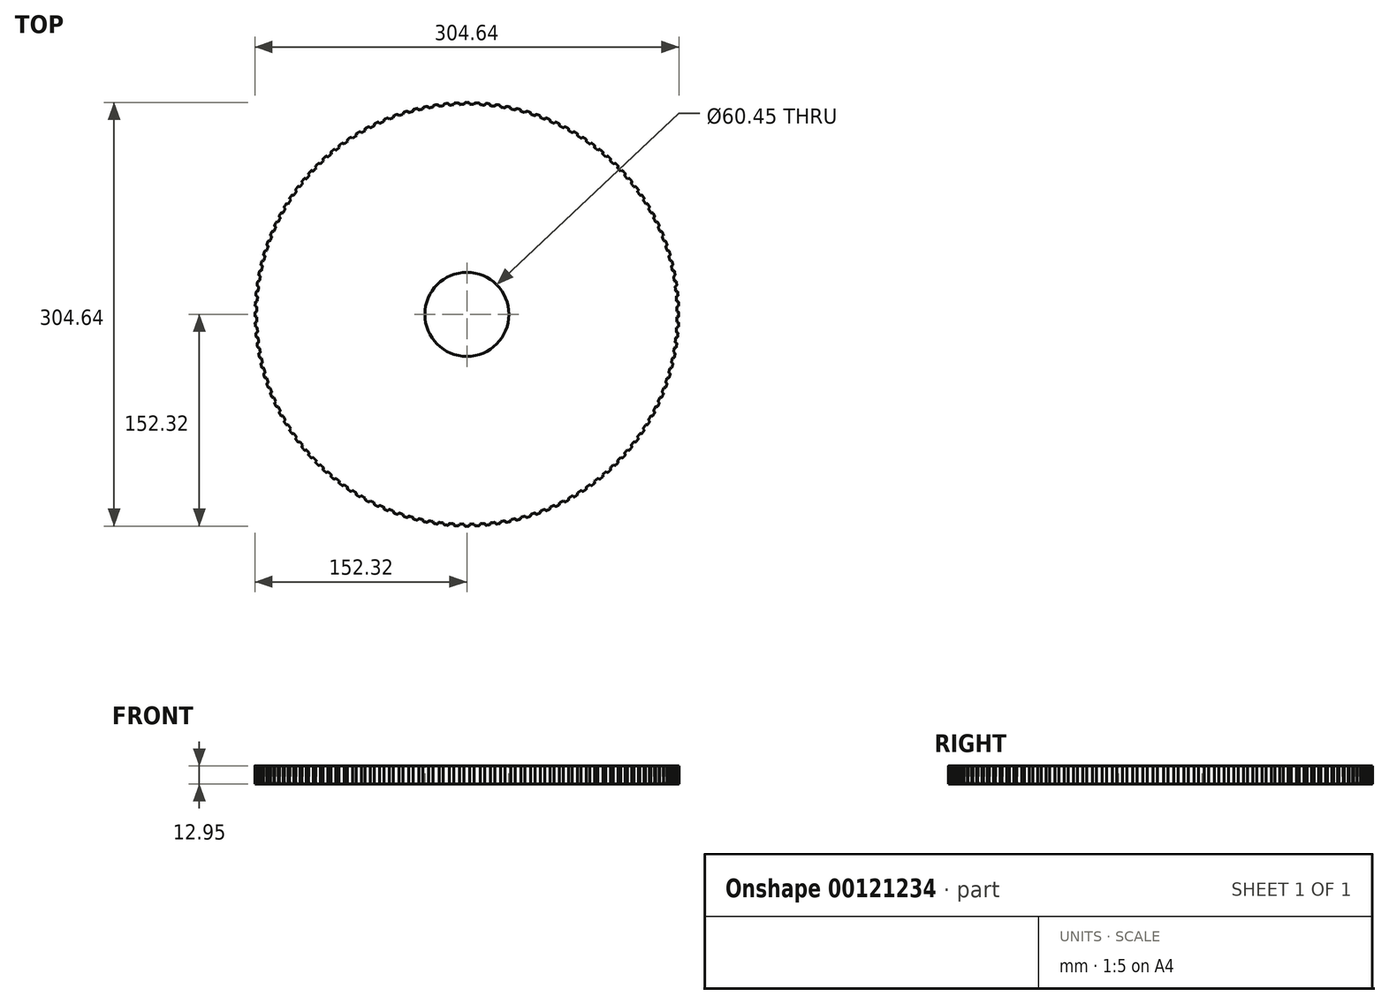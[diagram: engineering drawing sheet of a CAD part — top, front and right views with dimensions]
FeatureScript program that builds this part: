
annotation { "Feature Type Name" : "Feature", "Feature Type Description" : "" }
export const myFeature = defineFeature(function(context is Context, id is Id, definition is map)
    precondition{}
    {
        {
            var Q0;
            Q0=qCreatedBy(makeId("Top.planeOp"),FACE);
            var sketch = newSketch(context, id + "F0", { "sketchPlane" : qUnion([Q0])});
            skCircle(sketch, "E0", {"center": v(0, 0) * mm, "radius": 151 * mm});
            skSolve(sketch);
        }
        {
            var Q0;
            Q0 = qSketchRegion(id + "F0", true);
            extrude(context, id + "F1", {"entities" : qUnion([Q0]), "depth" : 12.95 * mm});
        }
        {
            var Q0;
            Q0=qCreatedBy(makeId("Top.planeOp"),FACE);
            var sketch = newSketch(context, id + "F2", { "sketchPlane" : qUnion([Q0])});
            skLineSegment(sketch, "E1", {"start": v(0, -0.08) * mm, "end": v(0, 183.08) * mm, "construction": true});
            skArc(sketch, "E2", {"start": v(1.26, 152.32) * mm, "mid": v(0, 152.32) * mm, "end": v(-1.26, 152.32) * mm});
            skLineSegment(sketch, "E3", {"start": v(-1.6, 152.1) * mm, "end": v(-2.1, 151.02) * mm});
            skLineSegment(sketch, "E4", {"start": v(1.6, 152.1) * mm, "end": v(2.1, 151.02) * mm});
            skPoint(sketch, "E5.visualSharp", {"position": v(-1.5, 152.32) * mm});
            skArc(sketch, "E5.filletArc", {"start": v(-1.26, 152.32) * mm, "mid": v(-1.46, 152.26) * mm, "end": v(-1.6, 152.1) * mm});
            skPoint(sketch, "E6.visualSharp", {"position": v(1.5, 152.32) * mm});
            skArc(sketch, "E6.filletArc", {"start": v(1.6, 152.1) * mm, "mid": v(1.46, 152.26) * mm, "end": v(1.26, 152.32) * mm});
            skArc(sketch, "E7", {"start": v(-2.27, 150.9) * mm, "mid": v(-2.17, 150.94) * mm, "end": v(-2.1, 151.02) * mm});
            skArc(sketch, "E8", {"start": v(2.1, 151.02) * mm, "mid": v(2.17, 150.94) * mm, "end": v(2.27, 150.9) * mm});
            skPoint(sketch, "E9.orphan", {"position": v(2.15, 150.91) * mm});
            skArc(sketch, "E10", {"start": v(-2.27, 150.9) * mm, "mid": v(0, 150.67) * mm, "end": v(2.27, 150.9) * mm});
            skSolve(sketch);
        }
        {
            var Q0;
            Q0=makeQuery(id+"F2.imprint","IMPRINT",FACE,{"disambiguationData":[TD([[makeQuery(id+"F2.imprint","IMPRINT",EDGE,{"derivedFrom":sQuery(id+"F2.wireOp",EDGE,"E2")}),1.0]])]});
            var Q1;
            Q1=makeQuery(id+"F2.imprint","IMPRINT",FACE,{"disambiguationData":[TD([[makeQuery(id+"F2.imprint","IMPRINT",EDGE,{"derivedFrom":sQuery(id+"F2.wireOp",EDGE,"bbfa1fc5-6552-4957-9194-8f10230bb92c.0")}),1.0]])]});
            var Q2;
            Q2=makeQuery(id+"F1.opExtrude","CAP_FACE",FACE,{"disambiguationData":[OSD([sQuery(id+"F0.wireOp",EDGE,"E0")])],"isStart":false});
            extrude(context, id + "F3", {"entities" : qUnion([Q0, Q1]), "endBound" : BoundingType.UP_TO_SURFACE, "endBoundEntityFace" : qUnion([Q2]), "depth" : 25.4 * mm});
        }
        {
            var Q0;
            Q0=qCreatedBy(makeId("Front.planeOp"),FACE);
            var sketch = newSketch(context, id + "F4", { "sketchPlane" : qUnion([Q0])});
            skLineSegment(sketch, "E11", {"start": v(0, 74.48) * mm, "end": v(0, -67.78) * mm, "construction": true});
            skSolve(sketch);
        }
        {
            var Q0;
            Q0=makeQuery(id+"F3.opExtrude","SWEPT_BODY",BODY,{"disambiguationData":[OSD([sQuery(id+"F2.wireOp",EDGE,"E2"),sQuery(id+"F2.wireOp",EDGE,"E3"),sQuery(id+"F2.wireOp",EDGE,"E4"),sQuery(id+"F2.wireOp",EDGE,"E5.filletArc"),sQuery(id+"F2.wireOp",EDGE,"E6.filletArc"),sQuery(id+"F2.wireOp",EDGE,"E7"),sQuery(id+"F2.wireOp",EDGE,"E8"),sQuery(id+"F2.wireOp",EDGE,"E10")])]});
            var Q1;
            Q1=sQuery(id+"F4.wireOp",EDGE,"E11");
            circularPattern(context, id + "F5", {"entities" : qUnion([Q0]), "axis" : qUnion([Q1]), "angle" : 360 * degree, "instanceCount" : 128, "equalSpace" : true});
        }
        {
            var Q0;
            Q0=makeQuery(id+"F1.opExtrude","SWEPT_BODY",BODY,{"disambiguationData":[OSD([sQuery(id+"F0.wireOp",EDGE,"E0")])]});
            var Q1;
            Q1=makeQuery(id+"F3.opExtrude","SWEPT_BODY",BODY,{"disambiguationData":[OSD([sQuery(id+"F2.wireOp",EDGE,"E2"),sQuery(id+"F2.wireOp",EDGE,"E3"),sQuery(id+"F2.wireOp",EDGE,"E4"),sQuery(id+"F2.wireOp",EDGE,"E5.filletArc"),sQuery(id+"F2.wireOp",EDGE,"E6.filletArc"),sQuery(id+"F2.wireOp",EDGE,"E7"),sQuery(id+"F2.wireOp",EDGE,"E8"),sQuery(id+"F2.wireOp",EDGE,"E10")])]});
            var Q2;
            Q2=makeQuery(id+"F5.opPattern","COPY",BODY,{"derivedFrom":makeQuery(id+"F3.opExtrude","SWEPT_BODY",BODY,{"disambiguationData":[OSD([sQuery(id+"F2.wireOp",EDGE,"E2"),sQuery(id+"F2.wireOp",EDGE,"E3"),sQuery(id+"F2.wireOp",EDGE,"E4"),sQuery(id+"F2.wireOp",EDGE,"E5.filletArc"),sQuery(id+"F2.wireOp",EDGE,"E6.filletArc"),sQuery(id+"F2.wireOp",EDGE,"E7"),sQuery(id+"F2.wireOp",EDGE,"E8"),sQuery(id+"F2.wireOp",EDGE,"E10")])]}),"instanceName":"1"});
            var Q3;
            Q3=makeQuery(id+"F5.opPattern","COPY",BODY,{"derivedFrom":makeQuery(id+"F3.opExtrude","SWEPT_BODY",BODY,{"disambiguationData":[OSD([sQuery(id+"F2.wireOp",EDGE,"E2"),sQuery(id+"F2.wireOp",EDGE,"E3"),sQuery(id+"F2.wireOp",EDGE,"E4"),sQuery(id+"F2.wireOp",EDGE,"E5.filletArc"),sQuery(id+"F2.wireOp",EDGE,"E6.filletArc"),sQuery(id+"F2.wireOp",EDGE,"E7"),sQuery(id+"F2.wireOp",EDGE,"E8"),sQuery(id+"F2.wireOp",EDGE,"E10")])]}),"instanceName":"2"});
            var Q4;
            Q4=makeQuery(id+"F5.opPattern","COPY",BODY,{"derivedFrom":makeQuery(id+"F3.opExtrude","SWEPT_BODY",BODY,{"disambiguationData":[OSD([sQuery(id+"F2.wireOp",EDGE,"E2"),sQuery(id+"F2.wireOp",EDGE,"E3"),sQuery(id+"F2.wireOp",EDGE,"E4"),sQuery(id+"F2.wireOp",EDGE,"E5.filletArc"),sQuery(id+"F2.wireOp",EDGE,"E6.filletArc"),sQuery(id+"F2.wireOp",EDGE,"E7"),sQuery(id+"F2.wireOp",EDGE,"E8"),sQuery(id+"F2.wireOp",EDGE,"E10")])]}),"instanceName":"3"});
            var Q5;
            Q5=makeQuery(id+"F5.opPattern","COPY",BODY,{"derivedFrom":makeQuery(id+"F3.opExtrude","SWEPT_BODY",BODY,{"disambiguationData":[OSD([sQuery(id+"F2.wireOp",EDGE,"E2"),sQuery(id+"F2.wireOp",EDGE,"E3"),sQuery(id+"F2.wireOp",EDGE,"E4"),sQuery(id+"F2.wireOp",EDGE,"E5.filletArc"),sQuery(id+"F2.wireOp",EDGE,"E6.filletArc"),sQuery(id+"F2.wireOp",EDGE,"E7"),sQuery(id+"F2.wireOp",EDGE,"E8"),sQuery(id+"F2.wireOp",EDGE,"E10")])]}),"instanceName":"4"});
            var Q6;
            Q6=makeQuery(id+"F5.opPattern","COPY",BODY,{"derivedFrom":makeQuery(id+"F3.opExtrude","SWEPT_BODY",BODY,{"disambiguationData":[OSD([sQuery(id+"F2.wireOp",EDGE,"E2"),sQuery(id+"F2.wireOp",EDGE,"E3"),sQuery(id+"F2.wireOp",EDGE,"E4"),sQuery(id+"F2.wireOp",EDGE,"E5.filletArc"),sQuery(id+"F2.wireOp",EDGE,"E6.filletArc"),sQuery(id+"F2.wireOp",EDGE,"E7"),sQuery(id+"F2.wireOp",EDGE,"E8"),sQuery(id+"F2.wireOp",EDGE,"E10")])]}),"instanceName":"5"});
            var Q7;
            Q7=makeQuery(id+"F5.opPattern","COPY",BODY,{"derivedFrom":makeQuery(id+"F3.opExtrude","SWEPT_BODY",BODY,{"disambiguationData":[OSD([sQuery(id+"F2.wireOp",EDGE,"E2"),sQuery(id+"F2.wireOp",EDGE,"E3"),sQuery(id+"F2.wireOp",EDGE,"E4"),sQuery(id+"F2.wireOp",EDGE,"E5.filletArc"),sQuery(id+"F2.wireOp",EDGE,"E6.filletArc"),sQuery(id+"F2.wireOp",EDGE,"E7"),sQuery(id+"F2.wireOp",EDGE,"E8"),sQuery(id+"F2.wireOp",EDGE,"E10")])]}),"instanceName":"6"});
            var Q8;
            Q8=makeQuery(id+"F5.opPattern","COPY",BODY,{"derivedFrom":makeQuery(id+"F3.opExtrude","SWEPT_BODY",BODY,{"disambiguationData":[OSD([sQuery(id+"F2.wireOp",EDGE,"E2"),sQuery(id+"F2.wireOp",EDGE,"E3"),sQuery(id+"F2.wireOp",EDGE,"E4"),sQuery(id+"F2.wireOp",EDGE,"E5.filletArc"),sQuery(id+"F2.wireOp",EDGE,"E6.filletArc"),sQuery(id+"F2.wireOp",EDGE,"E7"),sQuery(id+"F2.wireOp",EDGE,"E8"),sQuery(id+"F2.wireOp",EDGE,"E10")])]}),"instanceName":"7"});
            var Q9;
            Q9=makeQuery(id+"F5.opPattern","COPY",BODY,{"derivedFrom":makeQuery(id+"F3.opExtrude","SWEPT_BODY",BODY,{"disambiguationData":[OSD([sQuery(id+"F2.wireOp",EDGE,"E2"),sQuery(id+"F2.wireOp",EDGE,"E3"),sQuery(id+"F2.wireOp",EDGE,"E4"),sQuery(id+"F2.wireOp",EDGE,"E5.filletArc"),sQuery(id+"F2.wireOp",EDGE,"E6.filletArc"),sQuery(id+"F2.wireOp",EDGE,"E7"),sQuery(id+"F2.wireOp",EDGE,"E8"),sQuery(id+"F2.wireOp",EDGE,"E10")])]}),"instanceName":"8"});
            var Q10;
            Q10=makeQuery(id+"F5.opPattern","COPY",BODY,{"derivedFrom":makeQuery(id+"F3.opExtrude","SWEPT_BODY",BODY,{"disambiguationData":[OSD([sQuery(id+"F2.wireOp",EDGE,"E2"),sQuery(id+"F2.wireOp",EDGE,"E3"),sQuery(id+"F2.wireOp",EDGE,"E4"),sQuery(id+"F2.wireOp",EDGE,"E5.filletArc"),sQuery(id+"F2.wireOp",EDGE,"E6.filletArc"),sQuery(id+"F2.wireOp",EDGE,"E7"),sQuery(id+"F2.wireOp",EDGE,"E8"),sQuery(id+"F2.wireOp",EDGE,"E10")])]}),"instanceName":"9"});
            var Q11;
            Q11=makeQuery(id+"F5.opPattern","COPY",BODY,{"derivedFrom":makeQuery(id+"F3.opExtrude","SWEPT_BODY",BODY,{"disambiguationData":[OSD([sQuery(id+"F2.wireOp",EDGE,"E2"),sQuery(id+"F2.wireOp",EDGE,"E3"),sQuery(id+"F2.wireOp",EDGE,"E4"),sQuery(id+"F2.wireOp",EDGE,"E5.filletArc"),sQuery(id+"F2.wireOp",EDGE,"E6.filletArc"),sQuery(id+"F2.wireOp",EDGE,"E7"),sQuery(id+"F2.wireOp",EDGE,"E8"),sQuery(id+"F2.wireOp",EDGE,"E10")])]}),"instanceName":"10"});
            var Q12;
            Q12=makeQuery(id+"F5.opPattern","COPY",BODY,{"derivedFrom":makeQuery(id+"F3.opExtrude","SWEPT_BODY",BODY,{"disambiguationData":[OSD([sQuery(id+"F2.wireOp",EDGE,"E2"),sQuery(id+"F2.wireOp",EDGE,"E3"),sQuery(id+"F2.wireOp",EDGE,"E4"),sQuery(id+"F2.wireOp",EDGE,"E5.filletArc"),sQuery(id+"F2.wireOp",EDGE,"E6.filletArc"),sQuery(id+"F2.wireOp",EDGE,"E7"),sQuery(id+"F2.wireOp",EDGE,"E8"),sQuery(id+"F2.wireOp",EDGE,"E10")])]}),"instanceName":"11"});
            var Q13;
            Q13=makeQuery(id+"F5.opPattern","COPY",BODY,{"derivedFrom":makeQuery(id+"F3.opExtrude","SWEPT_BODY",BODY,{"disambiguationData":[OSD([sQuery(id+"F2.wireOp",EDGE,"E2"),sQuery(id+"F2.wireOp",EDGE,"E3"),sQuery(id+"F2.wireOp",EDGE,"E4"),sQuery(id+"F2.wireOp",EDGE,"E5.filletArc"),sQuery(id+"F2.wireOp",EDGE,"E6.filletArc"),sQuery(id+"F2.wireOp",EDGE,"E7"),sQuery(id+"F2.wireOp",EDGE,"E8"),sQuery(id+"F2.wireOp",EDGE,"E10")])]}),"instanceName":"12"});
            var Q14;
            Q14=makeQuery(id+"F5.opPattern","COPY",BODY,{"derivedFrom":makeQuery(id+"F3.opExtrude","SWEPT_BODY",BODY,{"disambiguationData":[OSD([sQuery(id+"F2.wireOp",EDGE,"E2"),sQuery(id+"F2.wireOp",EDGE,"E3"),sQuery(id+"F2.wireOp",EDGE,"E4"),sQuery(id+"F2.wireOp",EDGE,"E5.filletArc"),sQuery(id+"F2.wireOp",EDGE,"E6.filletArc"),sQuery(id+"F2.wireOp",EDGE,"E7"),sQuery(id+"F2.wireOp",EDGE,"E8"),sQuery(id+"F2.wireOp",EDGE,"E10")])]}),"instanceName":"13"});
            var Q15;
            Q15=makeQuery(id+"F5.opPattern","COPY",BODY,{"derivedFrom":makeQuery(id+"F3.opExtrude","SWEPT_BODY",BODY,{"disambiguationData":[OSD([sQuery(id+"F2.wireOp",EDGE,"E2"),sQuery(id+"F2.wireOp",EDGE,"E3"),sQuery(id+"F2.wireOp",EDGE,"E4"),sQuery(id+"F2.wireOp",EDGE,"E5.filletArc"),sQuery(id+"F2.wireOp",EDGE,"E6.filletArc"),sQuery(id+"F2.wireOp",EDGE,"E7"),sQuery(id+"F2.wireOp",EDGE,"E8"),sQuery(id+"F2.wireOp",EDGE,"E10")])]}),"instanceName":"14"});
            var Q16;
            Q16=makeQuery(id+"F5.opPattern","COPY",BODY,{"derivedFrom":makeQuery(id+"F3.opExtrude","SWEPT_BODY",BODY,{"disambiguationData":[OSD([sQuery(id+"F2.wireOp",EDGE,"E2"),sQuery(id+"F2.wireOp",EDGE,"E3"),sQuery(id+"F2.wireOp",EDGE,"E4"),sQuery(id+"F2.wireOp",EDGE,"E5.filletArc"),sQuery(id+"F2.wireOp",EDGE,"E6.filletArc"),sQuery(id+"F2.wireOp",EDGE,"E7"),sQuery(id+"F2.wireOp",EDGE,"E8"),sQuery(id+"F2.wireOp",EDGE,"E10")])]}),"instanceName":"15"});
            var Q17;
            Q17=makeQuery(id+"F5.opPattern","COPY",BODY,{"derivedFrom":makeQuery(id+"F3.opExtrude","SWEPT_BODY",BODY,{"disambiguationData":[OSD([sQuery(id+"F2.wireOp",EDGE,"E2"),sQuery(id+"F2.wireOp",EDGE,"E3"),sQuery(id+"F2.wireOp",EDGE,"E4"),sQuery(id+"F2.wireOp",EDGE,"E5.filletArc"),sQuery(id+"F2.wireOp",EDGE,"E6.filletArc"),sQuery(id+"F2.wireOp",EDGE,"E7"),sQuery(id+"F2.wireOp",EDGE,"E8"),sQuery(id+"F2.wireOp",EDGE,"E10")])]}),"instanceName":"16"});
            var Q18;
            Q18=makeQuery(id+"F5.opPattern","COPY",BODY,{"derivedFrom":makeQuery(id+"F3.opExtrude","SWEPT_BODY",BODY,{"disambiguationData":[OSD([sQuery(id+"F2.wireOp",EDGE,"E2"),sQuery(id+"F2.wireOp",EDGE,"E3"),sQuery(id+"F2.wireOp",EDGE,"E4"),sQuery(id+"F2.wireOp",EDGE,"E5.filletArc"),sQuery(id+"F2.wireOp",EDGE,"E6.filletArc"),sQuery(id+"F2.wireOp",EDGE,"E7"),sQuery(id+"F2.wireOp",EDGE,"E8"),sQuery(id+"F2.wireOp",EDGE,"E10")])]}),"instanceName":"17"});
            var Q19;
            Q19=makeQuery(id+"F5.opPattern","COPY",BODY,{"derivedFrom":makeQuery(id+"F3.opExtrude","SWEPT_BODY",BODY,{"disambiguationData":[OSD([sQuery(id+"F2.wireOp",EDGE,"E2"),sQuery(id+"F2.wireOp",EDGE,"E3"),sQuery(id+"F2.wireOp",EDGE,"E4"),sQuery(id+"F2.wireOp",EDGE,"E5.filletArc"),sQuery(id+"F2.wireOp",EDGE,"E6.filletArc"),sQuery(id+"F2.wireOp",EDGE,"E7"),sQuery(id+"F2.wireOp",EDGE,"E8"),sQuery(id+"F2.wireOp",EDGE,"E10")])]}),"instanceName":"18"});
            var Q20;
            Q20=makeQuery(id+"F5.opPattern","COPY",BODY,{"derivedFrom":makeQuery(id+"F3.opExtrude","SWEPT_BODY",BODY,{"disambiguationData":[OSD([sQuery(id+"F2.wireOp",EDGE,"E2"),sQuery(id+"F2.wireOp",EDGE,"E3"),sQuery(id+"F2.wireOp",EDGE,"E4"),sQuery(id+"F2.wireOp",EDGE,"E5.filletArc"),sQuery(id+"F2.wireOp",EDGE,"E6.filletArc"),sQuery(id+"F2.wireOp",EDGE,"E7"),sQuery(id+"F2.wireOp",EDGE,"E8"),sQuery(id+"F2.wireOp",EDGE,"E10")])]}),"instanceName":"19"});
            var Q21;
            Q21=makeQuery(id+"F5.opPattern","COPY",BODY,{"derivedFrom":makeQuery(id+"F3.opExtrude","SWEPT_BODY",BODY,{"disambiguationData":[OSD([sQuery(id+"F2.wireOp",EDGE,"E2"),sQuery(id+"F2.wireOp",EDGE,"E3"),sQuery(id+"F2.wireOp",EDGE,"E4"),sQuery(id+"F2.wireOp",EDGE,"E5.filletArc"),sQuery(id+"F2.wireOp",EDGE,"E6.filletArc"),sQuery(id+"F2.wireOp",EDGE,"E7"),sQuery(id+"F2.wireOp",EDGE,"E8"),sQuery(id+"F2.wireOp",EDGE,"E10")])]}),"instanceName":"20"});
            var Q22;
            Q22=makeQuery(id+"F5.opPattern","COPY",BODY,{"derivedFrom":makeQuery(id+"F3.opExtrude","SWEPT_BODY",BODY,{"disambiguationData":[OSD([sQuery(id+"F2.wireOp",EDGE,"E2"),sQuery(id+"F2.wireOp",EDGE,"E3"),sQuery(id+"F2.wireOp",EDGE,"E4"),sQuery(id+"F2.wireOp",EDGE,"E5.filletArc"),sQuery(id+"F2.wireOp",EDGE,"E6.filletArc"),sQuery(id+"F2.wireOp",EDGE,"E7"),sQuery(id+"F2.wireOp",EDGE,"E8"),sQuery(id+"F2.wireOp",EDGE,"E10")])]}),"instanceName":"21"});
            var Q23;
            Q23=makeQuery(id+"F5.opPattern","COPY",BODY,{"derivedFrom":makeQuery(id+"F3.opExtrude","SWEPT_BODY",BODY,{"disambiguationData":[OSD([sQuery(id+"F2.wireOp",EDGE,"E2"),sQuery(id+"F2.wireOp",EDGE,"E3"),sQuery(id+"F2.wireOp",EDGE,"E4"),sQuery(id+"F2.wireOp",EDGE,"E5.filletArc"),sQuery(id+"F2.wireOp",EDGE,"E6.filletArc"),sQuery(id+"F2.wireOp",EDGE,"E7"),sQuery(id+"F2.wireOp",EDGE,"E8"),sQuery(id+"F2.wireOp",EDGE,"E10")])]}),"instanceName":"22"});
            var Q24;
            Q24=makeQuery(id+"F5.opPattern","COPY",BODY,{"derivedFrom":makeQuery(id+"F3.opExtrude","SWEPT_BODY",BODY,{"disambiguationData":[OSD([sQuery(id+"F2.wireOp",EDGE,"E2"),sQuery(id+"F2.wireOp",EDGE,"E3"),sQuery(id+"F2.wireOp",EDGE,"E4"),sQuery(id+"F2.wireOp",EDGE,"E5.filletArc"),sQuery(id+"F2.wireOp",EDGE,"E6.filletArc"),sQuery(id+"F2.wireOp",EDGE,"E7"),sQuery(id+"F2.wireOp",EDGE,"E8"),sQuery(id+"F2.wireOp",EDGE,"E10")])]}),"instanceName":"23"});
            var Q25;
            Q25=makeQuery(id+"F5.opPattern","COPY",BODY,{"derivedFrom":makeQuery(id+"F3.opExtrude","SWEPT_BODY",BODY,{"disambiguationData":[OSD([sQuery(id+"F2.wireOp",EDGE,"E2"),sQuery(id+"F2.wireOp",EDGE,"E3"),sQuery(id+"F2.wireOp",EDGE,"E4"),sQuery(id+"F2.wireOp",EDGE,"E5.filletArc"),sQuery(id+"F2.wireOp",EDGE,"E6.filletArc"),sQuery(id+"F2.wireOp",EDGE,"E7"),sQuery(id+"F2.wireOp",EDGE,"E8"),sQuery(id+"F2.wireOp",EDGE,"E10")])]}),"instanceName":"24"});
            var Q26;
            Q26=makeQuery(id+"F5.opPattern","COPY",BODY,{"derivedFrom":makeQuery(id+"F3.opExtrude","SWEPT_BODY",BODY,{"disambiguationData":[OSD([sQuery(id+"F2.wireOp",EDGE,"E2"),sQuery(id+"F2.wireOp",EDGE,"E3"),sQuery(id+"F2.wireOp",EDGE,"E4"),sQuery(id+"F2.wireOp",EDGE,"E5.filletArc"),sQuery(id+"F2.wireOp",EDGE,"E6.filletArc"),sQuery(id+"F2.wireOp",EDGE,"E7"),sQuery(id+"F2.wireOp",EDGE,"E8"),sQuery(id+"F2.wireOp",EDGE,"E10")])]}),"instanceName":"25"});
            var Q27;
            Q27=makeQuery(id+"F5.opPattern","COPY",BODY,{"derivedFrom":makeQuery(id+"F3.opExtrude","SWEPT_BODY",BODY,{"disambiguationData":[OSD([sQuery(id+"F2.wireOp",EDGE,"E2"),sQuery(id+"F2.wireOp",EDGE,"E3"),sQuery(id+"F2.wireOp",EDGE,"E4"),sQuery(id+"F2.wireOp",EDGE,"E5.filletArc"),sQuery(id+"F2.wireOp",EDGE,"E6.filletArc"),sQuery(id+"F2.wireOp",EDGE,"E7"),sQuery(id+"F2.wireOp",EDGE,"E8"),sQuery(id+"F2.wireOp",EDGE,"E10")])]}),"instanceName":"26"});
            var Q28;
            Q28=makeQuery(id+"F5.opPattern","COPY",BODY,{"derivedFrom":makeQuery(id+"F3.opExtrude","SWEPT_BODY",BODY,{"disambiguationData":[OSD([sQuery(id+"F2.wireOp",EDGE,"E2"),sQuery(id+"F2.wireOp",EDGE,"E3"),sQuery(id+"F2.wireOp",EDGE,"E4"),sQuery(id+"F2.wireOp",EDGE,"E5.filletArc"),sQuery(id+"F2.wireOp",EDGE,"E6.filletArc"),sQuery(id+"F2.wireOp",EDGE,"E7"),sQuery(id+"F2.wireOp",EDGE,"E8"),sQuery(id+"F2.wireOp",EDGE,"E10")])]}),"instanceName":"27"});
            var Q29;
            Q29=makeQuery(id+"F5.opPattern","COPY",BODY,{"derivedFrom":makeQuery(id+"F3.opExtrude","SWEPT_BODY",BODY,{"disambiguationData":[OSD([sQuery(id+"F2.wireOp",EDGE,"E2"),sQuery(id+"F2.wireOp",EDGE,"E3"),sQuery(id+"F2.wireOp",EDGE,"E4"),sQuery(id+"F2.wireOp",EDGE,"E5.filletArc"),sQuery(id+"F2.wireOp",EDGE,"E6.filletArc"),sQuery(id+"F2.wireOp",EDGE,"E7"),sQuery(id+"F2.wireOp",EDGE,"E8"),sQuery(id+"F2.wireOp",EDGE,"E10")])]}),"instanceName":"28"});
            var Q30;
            Q30=makeQuery(id+"F5.opPattern","COPY",BODY,{"derivedFrom":makeQuery(id+"F3.opExtrude","SWEPT_BODY",BODY,{"disambiguationData":[OSD([sQuery(id+"F2.wireOp",EDGE,"E2"),sQuery(id+"F2.wireOp",EDGE,"E3"),sQuery(id+"F2.wireOp",EDGE,"E4"),sQuery(id+"F2.wireOp",EDGE,"E5.filletArc"),sQuery(id+"F2.wireOp",EDGE,"E6.filletArc"),sQuery(id+"F2.wireOp",EDGE,"E7"),sQuery(id+"F2.wireOp",EDGE,"E8"),sQuery(id+"F2.wireOp",EDGE,"E10")])]}),"instanceName":"29"});
            var Q31;
            Q31=makeQuery(id+"F5.opPattern","COPY",BODY,{"derivedFrom":makeQuery(id+"F3.opExtrude","SWEPT_BODY",BODY,{"disambiguationData":[OSD([sQuery(id+"F2.wireOp",EDGE,"E2"),sQuery(id+"F2.wireOp",EDGE,"E3"),sQuery(id+"F2.wireOp",EDGE,"E4"),sQuery(id+"F2.wireOp",EDGE,"E5.filletArc"),sQuery(id+"F2.wireOp",EDGE,"E6.filletArc"),sQuery(id+"F2.wireOp",EDGE,"E7"),sQuery(id+"F2.wireOp",EDGE,"E8"),sQuery(id+"F2.wireOp",EDGE,"E10")])]}),"instanceName":"30"});
            var Q32;
            Q32=makeQuery(id+"F5.opPattern","COPY",BODY,{"derivedFrom":makeQuery(id+"F3.opExtrude","SWEPT_BODY",BODY,{"disambiguationData":[OSD([sQuery(id+"F2.wireOp",EDGE,"E2"),sQuery(id+"F2.wireOp",EDGE,"E3"),sQuery(id+"F2.wireOp",EDGE,"E4"),sQuery(id+"F2.wireOp",EDGE,"E5.filletArc"),sQuery(id+"F2.wireOp",EDGE,"E6.filletArc"),sQuery(id+"F2.wireOp",EDGE,"E7"),sQuery(id+"F2.wireOp",EDGE,"E8"),sQuery(id+"F2.wireOp",EDGE,"E10")])]}),"instanceName":"31"});
            var Q33;
            Q33=makeQuery(id+"F5.opPattern","COPY",BODY,{"derivedFrom":makeQuery(id+"F3.opExtrude","SWEPT_BODY",BODY,{"disambiguationData":[OSD([sQuery(id+"F2.wireOp",EDGE,"E2"),sQuery(id+"F2.wireOp",EDGE,"E3"),sQuery(id+"F2.wireOp",EDGE,"E4"),sQuery(id+"F2.wireOp",EDGE,"E5.filletArc"),sQuery(id+"F2.wireOp",EDGE,"E6.filletArc"),sQuery(id+"F2.wireOp",EDGE,"E7"),sQuery(id+"F2.wireOp",EDGE,"E8"),sQuery(id+"F2.wireOp",EDGE,"E10")])]}),"instanceName":"32"});
            var Q34;
            Q34=makeQuery(id+"F5.opPattern","COPY",BODY,{"derivedFrom":makeQuery(id+"F3.opExtrude","SWEPT_BODY",BODY,{"disambiguationData":[OSD([sQuery(id+"F2.wireOp",EDGE,"E2"),sQuery(id+"F2.wireOp",EDGE,"E3"),sQuery(id+"F2.wireOp",EDGE,"E4"),sQuery(id+"F2.wireOp",EDGE,"E5.filletArc"),sQuery(id+"F2.wireOp",EDGE,"E6.filletArc"),sQuery(id+"F2.wireOp",EDGE,"E7"),sQuery(id+"F2.wireOp",EDGE,"E8"),sQuery(id+"F2.wireOp",EDGE,"E10")])]}),"instanceName":"33"});
            var Q35;
            Q35=makeQuery(id+"F5.opPattern","COPY",BODY,{"derivedFrom":makeQuery(id+"F3.opExtrude","SWEPT_BODY",BODY,{"disambiguationData":[OSD([sQuery(id+"F2.wireOp",EDGE,"E2"),sQuery(id+"F2.wireOp",EDGE,"E3"),sQuery(id+"F2.wireOp",EDGE,"E4"),sQuery(id+"F2.wireOp",EDGE,"E5.filletArc"),sQuery(id+"F2.wireOp",EDGE,"E6.filletArc"),sQuery(id+"F2.wireOp",EDGE,"E7"),sQuery(id+"F2.wireOp",EDGE,"E8"),sQuery(id+"F2.wireOp",EDGE,"E10")])]}),"instanceName":"34"});
            var Q36;
            Q36=makeQuery(id+"F5.opPattern","COPY",BODY,{"derivedFrom":makeQuery(id+"F3.opExtrude","SWEPT_BODY",BODY,{"disambiguationData":[OSD([sQuery(id+"F2.wireOp",EDGE,"E2"),sQuery(id+"F2.wireOp",EDGE,"E3"),sQuery(id+"F2.wireOp",EDGE,"E4"),sQuery(id+"F2.wireOp",EDGE,"E5.filletArc"),sQuery(id+"F2.wireOp",EDGE,"E6.filletArc"),sQuery(id+"F2.wireOp",EDGE,"E7"),sQuery(id+"F2.wireOp",EDGE,"E8"),sQuery(id+"F2.wireOp",EDGE,"E10")])]}),"instanceName":"35"});
            var Q37;
            Q37=makeQuery(id+"F5.opPattern","COPY",BODY,{"derivedFrom":makeQuery(id+"F3.opExtrude","SWEPT_BODY",BODY,{"disambiguationData":[OSD([sQuery(id+"F2.wireOp",EDGE,"E2"),sQuery(id+"F2.wireOp",EDGE,"E3"),sQuery(id+"F2.wireOp",EDGE,"E4"),sQuery(id+"F2.wireOp",EDGE,"E5.filletArc"),sQuery(id+"F2.wireOp",EDGE,"E6.filletArc"),sQuery(id+"F2.wireOp",EDGE,"E7"),sQuery(id+"F2.wireOp",EDGE,"E8"),sQuery(id+"F2.wireOp",EDGE,"E10")])]}),"instanceName":"36"});
            var Q38;
            Q38=makeQuery(id+"F5.opPattern","COPY",BODY,{"derivedFrom":makeQuery(id+"F3.opExtrude","SWEPT_BODY",BODY,{"disambiguationData":[OSD([sQuery(id+"F2.wireOp",EDGE,"E2"),sQuery(id+"F2.wireOp",EDGE,"E3"),sQuery(id+"F2.wireOp",EDGE,"E4"),sQuery(id+"F2.wireOp",EDGE,"E5.filletArc"),sQuery(id+"F2.wireOp",EDGE,"E6.filletArc"),sQuery(id+"F2.wireOp",EDGE,"E7"),sQuery(id+"F2.wireOp",EDGE,"E8"),sQuery(id+"F2.wireOp",EDGE,"E10")])]}),"instanceName":"37"});
            var Q39;
            Q39=makeQuery(id+"F5.opPattern","COPY",BODY,{"derivedFrom":makeQuery(id+"F3.opExtrude","SWEPT_BODY",BODY,{"disambiguationData":[OSD([sQuery(id+"F2.wireOp",EDGE,"E2"),sQuery(id+"F2.wireOp",EDGE,"E3"),sQuery(id+"F2.wireOp",EDGE,"E4"),sQuery(id+"F2.wireOp",EDGE,"E5.filletArc"),sQuery(id+"F2.wireOp",EDGE,"E6.filletArc"),sQuery(id+"F2.wireOp",EDGE,"E7"),sQuery(id+"F2.wireOp",EDGE,"E8"),sQuery(id+"F2.wireOp",EDGE,"E10")])]}),"instanceName":"38"});
            var Q40;
            Q40=makeQuery(id+"F5.opPattern","COPY",BODY,{"derivedFrom":makeQuery(id+"F3.opExtrude","SWEPT_BODY",BODY,{"disambiguationData":[OSD([sQuery(id+"F2.wireOp",EDGE,"E2"),sQuery(id+"F2.wireOp",EDGE,"E3"),sQuery(id+"F2.wireOp",EDGE,"E4"),sQuery(id+"F2.wireOp",EDGE,"E5.filletArc"),sQuery(id+"F2.wireOp",EDGE,"E6.filletArc"),sQuery(id+"F2.wireOp",EDGE,"E7"),sQuery(id+"F2.wireOp",EDGE,"E8"),sQuery(id+"F2.wireOp",EDGE,"E10")])]}),"instanceName":"39"});
            var Q41;
            Q41=makeQuery(id+"F5.opPattern","COPY",BODY,{"derivedFrom":makeQuery(id+"F3.opExtrude","SWEPT_BODY",BODY,{"disambiguationData":[OSD([sQuery(id+"F2.wireOp",EDGE,"E2"),sQuery(id+"F2.wireOp",EDGE,"E3"),sQuery(id+"F2.wireOp",EDGE,"E4"),sQuery(id+"F2.wireOp",EDGE,"E5.filletArc"),sQuery(id+"F2.wireOp",EDGE,"E6.filletArc"),sQuery(id+"F2.wireOp",EDGE,"E7"),sQuery(id+"F2.wireOp",EDGE,"E8"),sQuery(id+"F2.wireOp",EDGE,"E10")])]}),"instanceName":"40"});
            var Q42;
            Q42=makeQuery(id+"F5.opPattern","COPY",BODY,{"derivedFrom":makeQuery(id+"F3.opExtrude","SWEPT_BODY",BODY,{"disambiguationData":[OSD([sQuery(id+"F2.wireOp",EDGE,"E2"),sQuery(id+"F2.wireOp",EDGE,"E3"),sQuery(id+"F2.wireOp",EDGE,"E4"),sQuery(id+"F2.wireOp",EDGE,"E5.filletArc"),sQuery(id+"F2.wireOp",EDGE,"E6.filletArc"),sQuery(id+"F2.wireOp",EDGE,"E7"),sQuery(id+"F2.wireOp",EDGE,"E8"),sQuery(id+"F2.wireOp",EDGE,"E10")])]}),"instanceName":"41"});
            var Q43;
            Q43=makeQuery(id+"F5.opPattern","COPY",BODY,{"derivedFrom":makeQuery(id+"F3.opExtrude","SWEPT_BODY",BODY,{"disambiguationData":[OSD([sQuery(id+"F2.wireOp",EDGE,"E2"),sQuery(id+"F2.wireOp",EDGE,"E3"),sQuery(id+"F2.wireOp",EDGE,"E4"),sQuery(id+"F2.wireOp",EDGE,"E5.filletArc"),sQuery(id+"F2.wireOp",EDGE,"E6.filletArc"),sQuery(id+"F2.wireOp",EDGE,"E7"),sQuery(id+"F2.wireOp",EDGE,"E8"),sQuery(id+"F2.wireOp",EDGE,"E10")])]}),"instanceName":"42"});
            var Q44;
            Q44=makeQuery(id+"F5.opPattern","COPY",BODY,{"derivedFrom":makeQuery(id+"F3.opExtrude","SWEPT_BODY",BODY,{"disambiguationData":[OSD([sQuery(id+"F2.wireOp",EDGE,"E2"),sQuery(id+"F2.wireOp",EDGE,"E3"),sQuery(id+"F2.wireOp",EDGE,"E4"),sQuery(id+"F2.wireOp",EDGE,"E5.filletArc"),sQuery(id+"F2.wireOp",EDGE,"E6.filletArc"),sQuery(id+"F2.wireOp",EDGE,"E7"),sQuery(id+"F2.wireOp",EDGE,"E8"),sQuery(id+"F2.wireOp",EDGE,"E10")])]}),"instanceName":"43"});
            var Q45;
            Q45=makeQuery(id+"F5.opPattern","COPY",BODY,{"derivedFrom":makeQuery(id+"F3.opExtrude","SWEPT_BODY",BODY,{"disambiguationData":[OSD([sQuery(id+"F2.wireOp",EDGE,"E2"),sQuery(id+"F2.wireOp",EDGE,"E3"),sQuery(id+"F2.wireOp",EDGE,"E4"),sQuery(id+"F2.wireOp",EDGE,"E5.filletArc"),sQuery(id+"F2.wireOp",EDGE,"E6.filletArc"),sQuery(id+"F2.wireOp",EDGE,"E7"),sQuery(id+"F2.wireOp",EDGE,"E8"),sQuery(id+"F2.wireOp",EDGE,"E10")])]}),"instanceName":"44"});
            var Q46;
            Q46=makeQuery(id+"F5.opPattern","COPY",BODY,{"derivedFrom":makeQuery(id+"F3.opExtrude","SWEPT_BODY",BODY,{"disambiguationData":[OSD([sQuery(id+"F2.wireOp",EDGE,"E2"),sQuery(id+"F2.wireOp",EDGE,"E3"),sQuery(id+"F2.wireOp",EDGE,"E4"),sQuery(id+"F2.wireOp",EDGE,"E5.filletArc"),sQuery(id+"F2.wireOp",EDGE,"E6.filletArc"),sQuery(id+"F2.wireOp",EDGE,"E7"),sQuery(id+"F2.wireOp",EDGE,"E8"),sQuery(id+"F2.wireOp",EDGE,"E10")])]}),"instanceName":"45"});
            var Q47;
            Q47=makeQuery(id+"F5.opPattern","COPY",BODY,{"derivedFrom":makeQuery(id+"F3.opExtrude","SWEPT_BODY",BODY,{"disambiguationData":[OSD([sQuery(id+"F2.wireOp",EDGE,"E2"),sQuery(id+"F2.wireOp",EDGE,"E3"),sQuery(id+"F2.wireOp",EDGE,"E4"),sQuery(id+"F2.wireOp",EDGE,"E5.filletArc"),sQuery(id+"F2.wireOp",EDGE,"E6.filletArc"),sQuery(id+"F2.wireOp",EDGE,"E7"),sQuery(id+"F2.wireOp",EDGE,"E8"),sQuery(id+"F2.wireOp",EDGE,"E10")])]}),"instanceName":"46"});
            var Q48;
            Q48=makeQuery(id+"F5.opPattern","COPY",BODY,{"derivedFrom":makeQuery(id+"F3.opExtrude","SWEPT_BODY",BODY,{"disambiguationData":[OSD([sQuery(id+"F2.wireOp",EDGE,"E2"),sQuery(id+"F2.wireOp",EDGE,"E3"),sQuery(id+"F2.wireOp",EDGE,"E4"),sQuery(id+"F2.wireOp",EDGE,"E5.filletArc"),sQuery(id+"F2.wireOp",EDGE,"E6.filletArc"),sQuery(id+"F2.wireOp",EDGE,"E7"),sQuery(id+"F2.wireOp",EDGE,"E8"),sQuery(id+"F2.wireOp",EDGE,"E10")])]}),"instanceName":"47"});
            var Q49;
            Q49=makeQuery(id+"F5.opPattern","COPY",BODY,{"derivedFrom":makeQuery(id+"F3.opExtrude","SWEPT_BODY",BODY,{"disambiguationData":[OSD([sQuery(id+"F2.wireOp",EDGE,"E2"),sQuery(id+"F2.wireOp",EDGE,"E3"),sQuery(id+"F2.wireOp",EDGE,"E4"),sQuery(id+"F2.wireOp",EDGE,"E5.filletArc"),sQuery(id+"F2.wireOp",EDGE,"E6.filletArc"),sQuery(id+"F2.wireOp",EDGE,"E7"),sQuery(id+"F2.wireOp",EDGE,"E8"),sQuery(id+"F2.wireOp",EDGE,"E10")])]}),"instanceName":"48"});
            var Q50;
            Q50=makeQuery(id+"F5.opPattern","COPY",BODY,{"derivedFrom":makeQuery(id+"F3.opExtrude","SWEPT_BODY",BODY,{"disambiguationData":[OSD([sQuery(id+"F2.wireOp",EDGE,"E2"),sQuery(id+"F2.wireOp",EDGE,"E3"),sQuery(id+"F2.wireOp",EDGE,"E4"),sQuery(id+"F2.wireOp",EDGE,"E5.filletArc"),sQuery(id+"F2.wireOp",EDGE,"E6.filletArc"),sQuery(id+"F2.wireOp",EDGE,"E7"),sQuery(id+"F2.wireOp",EDGE,"E8"),sQuery(id+"F2.wireOp",EDGE,"E10")])]}),"instanceName":"49"});
            var Q51;
            Q51=makeQuery(id+"F5.opPattern","COPY",BODY,{"derivedFrom":makeQuery(id+"F3.opExtrude","SWEPT_BODY",BODY,{"disambiguationData":[OSD([sQuery(id+"F2.wireOp",EDGE,"E2"),sQuery(id+"F2.wireOp",EDGE,"E3"),sQuery(id+"F2.wireOp",EDGE,"E4"),sQuery(id+"F2.wireOp",EDGE,"E5.filletArc"),sQuery(id+"F2.wireOp",EDGE,"E6.filletArc"),sQuery(id+"F2.wireOp",EDGE,"E7"),sQuery(id+"F2.wireOp",EDGE,"E8"),sQuery(id+"F2.wireOp",EDGE,"E10")])]}),"instanceName":"50"});
            var Q52;
            Q52=makeQuery(id+"F5.opPattern","COPY",BODY,{"derivedFrom":makeQuery(id+"F3.opExtrude","SWEPT_BODY",BODY,{"disambiguationData":[OSD([sQuery(id+"F2.wireOp",EDGE,"E2"),sQuery(id+"F2.wireOp",EDGE,"E3"),sQuery(id+"F2.wireOp",EDGE,"E4"),sQuery(id+"F2.wireOp",EDGE,"E5.filletArc"),sQuery(id+"F2.wireOp",EDGE,"E6.filletArc"),sQuery(id+"F2.wireOp",EDGE,"E7"),sQuery(id+"F2.wireOp",EDGE,"E8"),sQuery(id+"F2.wireOp",EDGE,"E10")])]}),"instanceName":"51"});
            var Q53;
            Q53=makeQuery(id+"F5.opPattern","COPY",BODY,{"derivedFrom":makeQuery(id+"F3.opExtrude","SWEPT_BODY",BODY,{"disambiguationData":[OSD([sQuery(id+"F2.wireOp",EDGE,"E2"),sQuery(id+"F2.wireOp",EDGE,"E3"),sQuery(id+"F2.wireOp",EDGE,"E4"),sQuery(id+"F2.wireOp",EDGE,"E5.filletArc"),sQuery(id+"F2.wireOp",EDGE,"E6.filletArc"),sQuery(id+"F2.wireOp",EDGE,"E7"),sQuery(id+"F2.wireOp",EDGE,"E8"),sQuery(id+"F2.wireOp",EDGE,"E10")])]}),"instanceName":"52"});
            var Q54;
            Q54=makeQuery(id+"F5.opPattern","COPY",BODY,{"derivedFrom":makeQuery(id+"F3.opExtrude","SWEPT_BODY",BODY,{"disambiguationData":[OSD([sQuery(id+"F2.wireOp",EDGE,"E2"),sQuery(id+"F2.wireOp",EDGE,"E3"),sQuery(id+"F2.wireOp",EDGE,"E4"),sQuery(id+"F2.wireOp",EDGE,"E5.filletArc"),sQuery(id+"F2.wireOp",EDGE,"E6.filletArc"),sQuery(id+"F2.wireOp",EDGE,"E7"),sQuery(id+"F2.wireOp",EDGE,"E8"),sQuery(id+"F2.wireOp",EDGE,"E10")])]}),"instanceName":"53"});
            var Q55;
            Q55=makeQuery(id+"F5.opPattern","COPY",BODY,{"derivedFrom":makeQuery(id+"F3.opExtrude","SWEPT_BODY",BODY,{"disambiguationData":[OSD([sQuery(id+"F2.wireOp",EDGE,"E2"),sQuery(id+"F2.wireOp",EDGE,"E3"),sQuery(id+"F2.wireOp",EDGE,"E4"),sQuery(id+"F2.wireOp",EDGE,"E5.filletArc"),sQuery(id+"F2.wireOp",EDGE,"E6.filletArc"),sQuery(id+"F2.wireOp",EDGE,"E7"),sQuery(id+"F2.wireOp",EDGE,"E8"),sQuery(id+"F2.wireOp",EDGE,"E10")])]}),"instanceName":"54"});
            var Q56;
            Q56=makeQuery(id+"F5.opPattern","COPY",BODY,{"derivedFrom":makeQuery(id+"F3.opExtrude","SWEPT_BODY",BODY,{"disambiguationData":[OSD([sQuery(id+"F2.wireOp",EDGE,"E2"),sQuery(id+"F2.wireOp",EDGE,"E3"),sQuery(id+"F2.wireOp",EDGE,"E4"),sQuery(id+"F2.wireOp",EDGE,"E5.filletArc"),sQuery(id+"F2.wireOp",EDGE,"E6.filletArc"),sQuery(id+"F2.wireOp",EDGE,"E7"),sQuery(id+"F2.wireOp",EDGE,"E8"),sQuery(id+"F2.wireOp",EDGE,"E10")])]}),"instanceName":"55"});
            var Q57;
            Q57=makeQuery(id+"F5.opPattern","COPY",BODY,{"derivedFrom":makeQuery(id+"F3.opExtrude","SWEPT_BODY",BODY,{"disambiguationData":[OSD([sQuery(id+"F2.wireOp",EDGE,"E2"),sQuery(id+"F2.wireOp",EDGE,"E3"),sQuery(id+"F2.wireOp",EDGE,"E4"),sQuery(id+"F2.wireOp",EDGE,"E5.filletArc"),sQuery(id+"F2.wireOp",EDGE,"E6.filletArc"),sQuery(id+"F2.wireOp",EDGE,"E7"),sQuery(id+"F2.wireOp",EDGE,"E8"),sQuery(id+"F2.wireOp",EDGE,"E10")])]}),"instanceName":"56"});
            var Q58;
            Q58=makeQuery(id+"F5.opPattern","COPY",BODY,{"derivedFrom":makeQuery(id+"F3.opExtrude","SWEPT_BODY",BODY,{"disambiguationData":[OSD([sQuery(id+"F2.wireOp",EDGE,"E2"),sQuery(id+"F2.wireOp",EDGE,"E3"),sQuery(id+"F2.wireOp",EDGE,"E4"),sQuery(id+"F2.wireOp",EDGE,"E5.filletArc"),sQuery(id+"F2.wireOp",EDGE,"E6.filletArc"),sQuery(id+"F2.wireOp",EDGE,"E7"),sQuery(id+"F2.wireOp",EDGE,"E8"),sQuery(id+"F2.wireOp",EDGE,"E10")])]}),"instanceName":"57"});
            var Q59;
            Q59=makeQuery(id+"F5.opPattern","COPY",BODY,{"derivedFrom":makeQuery(id+"F3.opExtrude","SWEPT_BODY",BODY,{"disambiguationData":[OSD([sQuery(id+"F2.wireOp",EDGE,"E2"),sQuery(id+"F2.wireOp",EDGE,"E3"),sQuery(id+"F2.wireOp",EDGE,"E4"),sQuery(id+"F2.wireOp",EDGE,"E5.filletArc"),sQuery(id+"F2.wireOp",EDGE,"E6.filletArc"),sQuery(id+"F2.wireOp",EDGE,"E7"),sQuery(id+"F2.wireOp",EDGE,"E8"),sQuery(id+"F2.wireOp",EDGE,"E10")])]}),"instanceName":"58"});
            var Q60;
            Q60=makeQuery(id+"F5.opPattern","COPY",BODY,{"derivedFrom":makeQuery(id+"F3.opExtrude","SWEPT_BODY",BODY,{"disambiguationData":[OSD([sQuery(id+"F2.wireOp",EDGE,"E2"),sQuery(id+"F2.wireOp",EDGE,"E3"),sQuery(id+"F2.wireOp",EDGE,"E4"),sQuery(id+"F2.wireOp",EDGE,"E5.filletArc"),sQuery(id+"F2.wireOp",EDGE,"E6.filletArc"),sQuery(id+"F2.wireOp",EDGE,"E7"),sQuery(id+"F2.wireOp",EDGE,"E8"),sQuery(id+"F2.wireOp",EDGE,"E10")])]}),"instanceName":"59"});
            var Q61;
            Q61=makeQuery(id+"F5.opPattern","COPY",BODY,{"derivedFrom":makeQuery(id+"F3.opExtrude","SWEPT_BODY",BODY,{"disambiguationData":[OSD([sQuery(id+"F2.wireOp",EDGE,"E2"),sQuery(id+"F2.wireOp",EDGE,"E3"),sQuery(id+"F2.wireOp",EDGE,"E4"),sQuery(id+"F2.wireOp",EDGE,"E5.filletArc"),sQuery(id+"F2.wireOp",EDGE,"E6.filletArc"),sQuery(id+"F2.wireOp",EDGE,"E7"),sQuery(id+"F2.wireOp",EDGE,"E8"),sQuery(id+"F2.wireOp",EDGE,"E10")])]}),"instanceName":"60"});
            var Q62;
            Q62=makeQuery(id+"F5.opPattern","COPY",BODY,{"derivedFrom":makeQuery(id+"F3.opExtrude","SWEPT_BODY",BODY,{"disambiguationData":[OSD([sQuery(id+"F2.wireOp",EDGE,"E2"),sQuery(id+"F2.wireOp",EDGE,"E3"),sQuery(id+"F2.wireOp",EDGE,"E4"),sQuery(id+"F2.wireOp",EDGE,"E5.filletArc"),sQuery(id+"F2.wireOp",EDGE,"E6.filletArc"),sQuery(id+"F2.wireOp",EDGE,"E7"),sQuery(id+"F2.wireOp",EDGE,"E8"),sQuery(id+"F2.wireOp",EDGE,"E10")])]}),"instanceName":"61"});
            var Q63;
            Q63=makeQuery(id+"F5.opPattern","COPY",BODY,{"derivedFrom":makeQuery(id+"F3.opExtrude","SWEPT_BODY",BODY,{"disambiguationData":[OSD([sQuery(id+"F2.wireOp",EDGE,"E2"),sQuery(id+"F2.wireOp",EDGE,"E3"),sQuery(id+"F2.wireOp",EDGE,"E4"),sQuery(id+"F2.wireOp",EDGE,"E5.filletArc"),sQuery(id+"F2.wireOp",EDGE,"E6.filletArc"),sQuery(id+"F2.wireOp",EDGE,"E7"),sQuery(id+"F2.wireOp",EDGE,"E8"),sQuery(id+"F2.wireOp",EDGE,"E10")])]}),"instanceName":"62"});
            var Q64;
            Q64=makeQuery(id+"F5.opPattern","COPY",BODY,{"derivedFrom":makeQuery(id+"F3.opExtrude","SWEPT_BODY",BODY,{"disambiguationData":[OSD([sQuery(id+"F2.wireOp",EDGE,"E2"),sQuery(id+"F2.wireOp",EDGE,"E3"),sQuery(id+"F2.wireOp",EDGE,"E4"),sQuery(id+"F2.wireOp",EDGE,"E5.filletArc"),sQuery(id+"F2.wireOp",EDGE,"E6.filletArc"),sQuery(id+"F2.wireOp",EDGE,"E7"),sQuery(id+"F2.wireOp",EDGE,"E8"),sQuery(id+"F2.wireOp",EDGE,"E10")])]}),"instanceName":"63"});
            var Q65;
            Q65=makeQuery(id+"F5.opPattern","COPY",BODY,{"derivedFrom":makeQuery(id+"F3.opExtrude","SWEPT_BODY",BODY,{"disambiguationData":[OSD([sQuery(id+"F2.wireOp",EDGE,"E2"),sQuery(id+"F2.wireOp",EDGE,"E3"),sQuery(id+"F2.wireOp",EDGE,"E4"),sQuery(id+"F2.wireOp",EDGE,"E5.filletArc"),sQuery(id+"F2.wireOp",EDGE,"E6.filletArc"),sQuery(id+"F2.wireOp",EDGE,"E7"),sQuery(id+"F2.wireOp",EDGE,"E8"),sQuery(id+"F2.wireOp",EDGE,"E10")])]}),"instanceName":"64"});
            var Q66;
            Q66=makeQuery(id+"F5.opPattern","COPY",BODY,{"derivedFrom":makeQuery(id+"F3.opExtrude","SWEPT_BODY",BODY,{"disambiguationData":[OSD([sQuery(id+"F2.wireOp",EDGE,"E2"),sQuery(id+"F2.wireOp",EDGE,"E3"),sQuery(id+"F2.wireOp",EDGE,"E4"),sQuery(id+"F2.wireOp",EDGE,"E5.filletArc"),sQuery(id+"F2.wireOp",EDGE,"E6.filletArc"),sQuery(id+"F2.wireOp",EDGE,"E7"),sQuery(id+"F2.wireOp",EDGE,"E8"),sQuery(id+"F2.wireOp",EDGE,"E10")])]}),"instanceName":"65"});
            var Q67;
            Q67=makeQuery(id+"F5.opPattern","COPY",BODY,{"derivedFrom":makeQuery(id+"F3.opExtrude","SWEPT_BODY",BODY,{"disambiguationData":[OSD([sQuery(id+"F2.wireOp",EDGE,"E2"),sQuery(id+"F2.wireOp",EDGE,"E3"),sQuery(id+"F2.wireOp",EDGE,"E4"),sQuery(id+"F2.wireOp",EDGE,"E5.filletArc"),sQuery(id+"F2.wireOp",EDGE,"E6.filletArc"),sQuery(id+"F2.wireOp",EDGE,"E7"),sQuery(id+"F2.wireOp",EDGE,"E8"),sQuery(id+"F2.wireOp",EDGE,"E10")])]}),"instanceName":"66"});
            var Q68;
            Q68=makeQuery(id+"F5.opPattern","COPY",BODY,{"derivedFrom":makeQuery(id+"F3.opExtrude","SWEPT_BODY",BODY,{"disambiguationData":[OSD([sQuery(id+"F2.wireOp",EDGE,"E2"),sQuery(id+"F2.wireOp",EDGE,"E3"),sQuery(id+"F2.wireOp",EDGE,"E4"),sQuery(id+"F2.wireOp",EDGE,"E5.filletArc"),sQuery(id+"F2.wireOp",EDGE,"E6.filletArc"),sQuery(id+"F2.wireOp",EDGE,"E7"),sQuery(id+"F2.wireOp",EDGE,"E8"),sQuery(id+"F2.wireOp",EDGE,"E10")])]}),"instanceName":"67"});
            var Q69;
            Q69=makeQuery(id+"F5.opPattern","COPY",BODY,{"derivedFrom":makeQuery(id+"F3.opExtrude","SWEPT_BODY",BODY,{"disambiguationData":[OSD([sQuery(id+"F2.wireOp",EDGE,"E2"),sQuery(id+"F2.wireOp",EDGE,"E3"),sQuery(id+"F2.wireOp",EDGE,"E4"),sQuery(id+"F2.wireOp",EDGE,"E5.filletArc"),sQuery(id+"F2.wireOp",EDGE,"E6.filletArc"),sQuery(id+"F2.wireOp",EDGE,"E7"),sQuery(id+"F2.wireOp",EDGE,"E8"),sQuery(id+"F2.wireOp",EDGE,"E10")])]}),"instanceName":"68"});
            var Q70;
            Q70=makeQuery(id+"F5.opPattern","COPY",BODY,{"derivedFrom":makeQuery(id+"F3.opExtrude","SWEPT_BODY",BODY,{"disambiguationData":[OSD([sQuery(id+"F2.wireOp",EDGE,"E2"),sQuery(id+"F2.wireOp",EDGE,"E3"),sQuery(id+"F2.wireOp",EDGE,"E4"),sQuery(id+"F2.wireOp",EDGE,"E5.filletArc"),sQuery(id+"F2.wireOp",EDGE,"E6.filletArc"),sQuery(id+"F2.wireOp",EDGE,"E7"),sQuery(id+"F2.wireOp",EDGE,"E8"),sQuery(id+"F2.wireOp",EDGE,"E10")])]}),"instanceName":"69"});
            var Q71;
            Q71=makeQuery(id+"F5.opPattern","COPY",BODY,{"derivedFrom":makeQuery(id+"F3.opExtrude","SWEPT_BODY",BODY,{"disambiguationData":[OSD([sQuery(id+"F2.wireOp",EDGE,"E2"),sQuery(id+"F2.wireOp",EDGE,"E3"),sQuery(id+"F2.wireOp",EDGE,"E4"),sQuery(id+"F2.wireOp",EDGE,"E5.filletArc"),sQuery(id+"F2.wireOp",EDGE,"E6.filletArc"),sQuery(id+"F2.wireOp",EDGE,"E7"),sQuery(id+"F2.wireOp",EDGE,"E8"),sQuery(id+"F2.wireOp",EDGE,"E10")])]}),"instanceName":"70"});
            var Q72;
            Q72=makeQuery(id+"F5.opPattern","COPY",BODY,{"derivedFrom":makeQuery(id+"F3.opExtrude","SWEPT_BODY",BODY,{"disambiguationData":[OSD([sQuery(id+"F2.wireOp",EDGE,"E2"),sQuery(id+"F2.wireOp",EDGE,"E3"),sQuery(id+"F2.wireOp",EDGE,"E4"),sQuery(id+"F2.wireOp",EDGE,"E5.filletArc"),sQuery(id+"F2.wireOp",EDGE,"E6.filletArc"),sQuery(id+"F2.wireOp",EDGE,"E7"),sQuery(id+"F2.wireOp",EDGE,"E8"),sQuery(id+"F2.wireOp",EDGE,"E10")])]}),"instanceName":"71"});
            var Q73;
            Q73=makeQuery(id+"F5.opPattern","COPY",BODY,{"derivedFrom":makeQuery(id+"F3.opExtrude","SWEPT_BODY",BODY,{"disambiguationData":[OSD([sQuery(id+"F2.wireOp",EDGE,"E2"),sQuery(id+"F2.wireOp",EDGE,"E3"),sQuery(id+"F2.wireOp",EDGE,"E4"),sQuery(id+"F2.wireOp",EDGE,"E5.filletArc"),sQuery(id+"F2.wireOp",EDGE,"E6.filletArc"),sQuery(id+"F2.wireOp",EDGE,"E7"),sQuery(id+"F2.wireOp",EDGE,"E8"),sQuery(id+"F2.wireOp",EDGE,"E10")])]}),"instanceName":"72"});
            var Q74;
            Q74=makeQuery(id+"F5.opPattern","COPY",BODY,{"derivedFrom":makeQuery(id+"F3.opExtrude","SWEPT_BODY",BODY,{"disambiguationData":[OSD([sQuery(id+"F2.wireOp",EDGE,"E2"),sQuery(id+"F2.wireOp",EDGE,"E3"),sQuery(id+"F2.wireOp",EDGE,"E4"),sQuery(id+"F2.wireOp",EDGE,"E5.filletArc"),sQuery(id+"F2.wireOp",EDGE,"E6.filletArc"),sQuery(id+"F2.wireOp",EDGE,"E7"),sQuery(id+"F2.wireOp",EDGE,"E8"),sQuery(id+"F2.wireOp",EDGE,"E10")])]}),"instanceName":"73"});
            var Q75;
            Q75=makeQuery(id+"F5.opPattern","COPY",BODY,{"derivedFrom":makeQuery(id+"F3.opExtrude","SWEPT_BODY",BODY,{"disambiguationData":[OSD([sQuery(id+"F2.wireOp",EDGE,"E2"),sQuery(id+"F2.wireOp",EDGE,"E3"),sQuery(id+"F2.wireOp",EDGE,"E4"),sQuery(id+"F2.wireOp",EDGE,"E5.filletArc"),sQuery(id+"F2.wireOp",EDGE,"E6.filletArc"),sQuery(id+"F2.wireOp",EDGE,"E7"),sQuery(id+"F2.wireOp",EDGE,"E8"),sQuery(id+"F2.wireOp",EDGE,"E10")])]}),"instanceName":"74"});
            var Q76;
            Q76=makeQuery(id+"F5.opPattern","COPY",BODY,{"derivedFrom":makeQuery(id+"F3.opExtrude","SWEPT_BODY",BODY,{"disambiguationData":[OSD([sQuery(id+"F2.wireOp",EDGE,"E2"),sQuery(id+"F2.wireOp",EDGE,"E3"),sQuery(id+"F2.wireOp",EDGE,"E4"),sQuery(id+"F2.wireOp",EDGE,"E5.filletArc"),sQuery(id+"F2.wireOp",EDGE,"E6.filletArc"),sQuery(id+"F2.wireOp",EDGE,"E7"),sQuery(id+"F2.wireOp",EDGE,"E8"),sQuery(id+"F2.wireOp",EDGE,"E10")])]}),"instanceName":"75"});
            var Q77;
            Q77=makeQuery(id+"F5.opPattern","COPY",BODY,{"derivedFrom":makeQuery(id+"F3.opExtrude","SWEPT_BODY",BODY,{"disambiguationData":[OSD([sQuery(id+"F2.wireOp",EDGE,"E2"),sQuery(id+"F2.wireOp",EDGE,"E3"),sQuery(id+"F2.wireOp",EDGE,"E4"),sQuery(id+"F2.wireOp",EDGE,"E5.filletArc"),sQuery(id+"F2.wireOp",EDGE,"E6.filletArc"),sQuery(id+"F2.wireOp",EDGE,"E7"),sQuery(id+"F2.wireOp",EDGE,"E8"),sQuery(id+"F2.wireOp",EDGE,"E10")])]}),"instanceName":"76"});
            var Q78;
            Q78=makeQuery(id+"F5.opPattern","COPY",BODY,{"derivedFrom":makeQuery(id+"F3.opExtrude","SWEPT_BODY",BODY,{"disambiguationData":[OSD([sQuery(id+"F2.wireOp",EDGE,"E2"),sQuery(id+"F2.wireOp",EDGE,"E3"),sQuery(id+"F2.wireOp",EDGE,"E4"),sQuery(id+"F2.wireOp",EDGE,"E5.filletArc"),sQuery(id+"F2.wireOp",EDGE,"E6.filletArc"),sQuery(id+"F2.wireOp",EDGE,"E7"),sQuery(id+"F2.wireOp",EDGE,"E8"),sQuery(id+"F2.wireOp",EDGE,"E10")])]}),"instanceName":"77"});
            var Q79;
            Q79=makeQuery(id+"F5.opPattern","COPY",BODY,{"derivedFrom":makeQuery(id+"F3.opExtrude","SWEPT_BODY",BODY,{"disambiguationData":[OSD([sQuery(id+"F2.wireOp",EDGE,"E2"),sQuery(id+"F2.wireOp",EDGE,"E3"),sQuery(id+"F2.wireOp",EDGE,"E4"),sQuery(id+"F2.wireOp",EDGE,"E5.filletArc"),sQuery(id+"F2.wireOp",EDGE,"E6.filletArc"),sQuery(id+"F2.wireOp",EDGE,"E7"),sQuery(id+"F2.wireOp",EDGE,"E8"),sQuery(id+"F2.wireOp",EDGE,"E10")])]}),"instanceName":"78"});
            var Q80;
            Q80=makeQuery(id+"F5.opPattern","COPY",BODY,{"derivedFrom":makeQuery(id+"F3.opExtrude","SWEPT_BODY",BODY,{"disambiguationData":[OSD([sQuery(id+"F2.wireOp",EDGE,"E2"),sQuery(id+"F2.wireOp",EDGE,"E3"),sQuery(id+"F2.wireOp",EDGE,"E4"),sQuery(id+"F2.wireOp",EDGE,"E5.filletArc"),sQuery(id+"F2.wireOp",EDGE,"E6.filletArc"),sQuery(id+"F2.wireOp",EDGE,"E7"),sQuery(id+"F2.wireOp",EDGE,"E8"),sQuery(id+"F2.wireOp",EDGE,"E10")])]}),"instanceName":"79"});
            var Q81;
            Q81=makeQuery(id+"F5.opPattern","COPY",BODY,{"derivedFrom":makeQuery(id+"F3.opExtrude","SWEPT_BODY",BODY,{"disambiguationData":[OSD([sQuery(id+"F2.wireOp",EDGE,"E2"),sQuery(id+"F2.wireOp",EDGE,"E3"),sQuery(id+"F2.wireOp",EDGE,"E4"),sQuery(id+"F2.wireOp",EDGE,"E5.filletArc"),sQuery(id+"F2.wireOp",EDGE,"E6.filletArc"),sQuery(id+"F2.wireOp",EDGE,"E7"),sQuery(id+"F2.wireOp",EDGE,"E8"),sQuery(id+"F2.wireOp",EDGE,"E10")])]}),"instanceName":"80"});
            var Q82;
            Q82=makeQuery(id+"F5.opPattern","COPY",BODY,{"derivedFrom":makeQuery(id+"F3.opExtrude","SWEPT_BODY",BODY,{"disambiguationData":[OSD([sQuery(id+"F2.wireOp",EDGE,"E2"),sQuery(id+"F2.wireOp",EDGE,"E3"),sQuery(id+"F2.wireOp",EDGE,"E4"),sQuery(id+"F2.wireOp",EDGE,"E5.filletArc"),sQuery(id+"F2.wireOp",EDGE,"E6.filletArc"),sQuery(id+"F2.wireOp",EDGE,"E7"),sQuery(id+"F2.wireOp",EDGE,"E8"),sQuery(id+"F2.wireOp",EDGE,"E10")])]}),"instanceName":"81"});
            var Q83;
            Q83=makeQuery(id+"F5.opPattern","COPY",BODY,{"derivedFrom":makeQuery(id+"F3.opExtrude","SWEPT_BODY",BODY,{"disambiguationData":[OSD([sQuery(id+"F2.wireOp",EDGE,"E2"),sQuery(id+"F2.wireOp",EDGE,"E3"),sQuery(id+"F2.wireOp",EDGE,"E4"),sQuery(id+"F2.wireOp",EDGE,"E5.filletArc"),sQuery(id+"F2.wireOp",EDGE,"E6.filletArc"),sQuery(id+"F2.wireOp",EDGE,"E7"),sQuery(id+"F2.wireOp",EDGE,"E8"),sQuery(id+"F2.wireOp",EDGE,"E10")])]}),"instanceName":"82"});
            var Q84;
            Q84=makeQuery(id+"F5.opPattern","COPY",BODY,{"derivedFrom":makeQuery(id+"F3.opExtrude","SWEPT_BODY",BODY,{"disambiguationData":[OSD([sQuery(id+"F2.wireOp",EDGE,"E2"),sQuery(id+"F2.wireOp",EDGE,"E3"),sQuery(id+"F2.wireOp",EDGE,"E4"),sQuery(id+"F2.wireOp",EDGE,"E5.filletArc"),sQuery(id+"F2.wireOp",EDGE,"E6.filletArc"),sQuery(id+"F2.wireOp",EDGE,"E7"),sQuery(id+"F2.wireOp",EDGE,"E8"),sQuery(id+"F2.wireOp",EDGE,"E10")])]}),"instanceName":"83"});
            var Q85;
            Q85=makeQuery(id+"F5.opPattern","COPY",BODY,{"derivedFrom":makeQuery(id+"F3.opExtrude","SWEPT_BODY",BODY,{"disambiguationData":[OSD([sQuery(id+"F2.wireOp",EDGE,"E2"),sQuery(id+"F2.wireOp",EDGE,"E3"),sQuery(id+"F2.wireOp",EDGE,"E4"),sQuery(id+"F2.wireOp",EDGE,"E5.filletArc"),sQuery(id+"F2.wireOp",EDGE,"E6.filletArc"),sQuery(id+"F2.wireOp",EDGE,"E7"),sQuery(id+"F2.wireOp",EDGE,"E8"),sQuery(id+"F2.wireOp",EDGE,"E10")])]}),"instanceName":"84"});
            var Q86;
            Q86=makeQuery(id+"F5.opPattern","COPY",BODY,{"derivedFrom":makeQuery(id+"F3.opExtrude","SWEPT_BODY",BODY,{"disambiguationData":[OSD([sQuery(id+"F2.wireOp",EDGE,"E2"),sQuery(id+"F2.wireOp",EDGE,"E3"),sQuery(id+"F2.wireOp",EDGE,"E4"),sQuery(id+"F2.wireOp",EDGE,"E5.filletArc"),sQuery(id+"F2.wireOp",EDGE,"E6.filletArc"),sQuery(id+"F2.wireOp",EDGE,"E7"),sQuery(id+"F2.wireOp",EDGE,"E8"),sQuery(id+"F2.wireOp",EDGE,"E10")])]}),"instanceName":"85"});
            var Q87;
            Q87=makeQuery(id+"F5.opPattern","COPY",BODY,{"derivedFrom":makeQuery(id+"F3.opExtrude","SWEPT_BODY",BODY,{"disambiguationData":[OSD([sQuery(id+"F2.wireOp",EDGE,"E2"),sQuery(id+"F2.wireOp",EDGE,"E3"),sQuery(id+"F2.wireOp",EDGE,"E4"),sQuery(id+"F2.wireOp",EDGE,"E5.filletArc"),sQuery(id+"F2.wireOp",EDGE,"E6.filletArc"),sQuery(id+"F2.wireOp",EDGE,"E7"),sQuery(id+"F2.wireOp",EDGE,"E8"),sQuery(id+"F2.wireOp",EDGE,"E10")])]}),"instanceName":"86"});
            var Q88;
            Q88=makeQuery(id+"F5.opPattern","COPY",BODY,{"derivedFrom":makeQuery(id+"F3.opExtrude","SWEPT_BODY",BODY,{"disambiguationData":[OSD([sQuery(id+"F2.wireOp",EDGE,"E2"),sQuery(id+"F2.wireOp",EDGE,"E3"),sQuery(id+"F2.wireOp",EDGE,"E4"),sQuery(id+"F2.wireOp",EDGE,"E5.filletArc"),sQuery(id+"F2.wireOp",EDGE,"E6.filletArc"),sQuery(id+"F2.wireOp",EDGE,"E7"),sQuery(id+"F2.wireOp",EDGE,"E8"),sQuery(id+"F2.wireOp",EDGE,"E10")])]}),"instanceName":"87"});
            var Q89;
            Q89=makeQuery(id+"F5.opPattern","COPY",BODY,{"derivedFrom":makeQuery(id+"F3.opExtrude","SWEPT_BODY",BODY,{"disambiguationData":[OSD([sQuery(id+"F2.wireOp",EDGE,"E2"),sQuery(id+"F2.wireOp",EDGE,"E3"),sQuery(id+"F2.wireOp",EDGE,"E4"),sQuery(id+"F2.wireOp",EDGE,"E5.filletArc"),sQuery(id+"F2.wireOp",EDGE,"E6.filletArc"),sQuery(id+"F2.wireOp",EDGE,"E7"),sQuery(id+"F2.wireOp",EDGE,"E8"),sQuery(id+"F2.wireOp",EDGE,"E10")])]}),"instanceName":"88"});
            var Q90;
            Q90=makeQuery(id+"F5.opPattern","COPY",BODY,{"derivedFrom":makeQuery(id+"F3.opExtrude","SWEPT_BODY",BODY,{"disambiguationData":[OSD([sQuery(id+"F2.wireOp",EDGE,"E2"),sQuery(id+"F2.wireOp",EDGE,"E3"),sQuery(id+"F2.wireOp",EDGE,"E4"),sQuery(id+"F2.wireOp",EDGE,"E5.filletArc"),sQuery(id+"F2.wireOp",EDGE,"E6.filletArc"),sQuery(id+"F2.wireOp",EDGE,"E7"),sQuery(id+"F2.wireOp",EDGE,"E8"),sQuery(id+"F2.wireOp",EDGE,"E10")])]}),"instanceName":"89"});
            var Q91;
            Q91=makeQuery(id+"F5.opPattern","COPY",BODY,{"derivedFrom":makeQuery(id+"F3.opExtrude","SWEPT_BODY",BODY,{"disambiguationData":[OSD([sQuery(id+"F2.wireOp",EDGE,"E2"),sQuery(id+"F2.wireOp",EDGE,"E3"),sQuery(id+"F2.wireOp",EDGE,"E4"),sQuery(id+"F2.wireOp",EDGE,"E5.filletArc"),sQuery(id+"F2.wireOp",EDGE,"E6.filletArc"),sQuery(id+"F2.wireOp",EDGE,"E7"),sQuery(id+"F2.wireOp",EDGE,"E8"),sQuery(id+"F2.wireOp",EDGE,"E10")])]}),"instanceName":"90"});
            var Q92;
            Q92=makeQuery(id+"F5.opPattern","COPY",BODY,{"derivedFrom":makeQuery(id+"F3.opExtrude","SWEPT_BODY",BODY,{"disambiguationData":[OSD([sQuery(id+"F2.wireOp",EDGE,"E2"),sQuery(id+"F2.wireOp",EDGE,"E3"),sQuery(id+"F2.wireOp",EDGE,"E4"),sQuery(id+"F2.wireOp",EDGE,"E5.filletArc"),sQuery(id+"F2.wireOp",EDGE,"E6.filletArc"),sQuery(id+"F2.wireOp",EDGE,"E7"),sQuery(id+"F2.wireOp",EDGE,"E8"),sQuery(id+"F2.wireOp",EDGE,"E10")])]}),"instanceName":"91"});
            var Q93;
            Q93=makeQuery(id+"F5.opPattern","COPY",BODY,{"derivedFrom":makeQuery(id+"F3.opExtrude","SWEPT_BODY",BODY,{"disambiguationData":[OSD([sQuery(id+"F2.wireOp",EDGE,"E2"),sQuery(id+"F2.wireOp",EDGE,"E3"),sQuery(id+"F2.wireOp",EDGE,"E4"),sQuery(id+"F2.wireOp",EDGE,"E5.filletArc"),sQuery(id+"F2.wireOp",EDGE,"E6.filletArc"),sQuery(id+"F2.wireOp",EDGE,"E7"),sQuery(id+"F2.wireOp",EDGE,"E8"),sQuery(id+"F2.wireOp",EDGE,"E10")])]}),"instanceName":"92"});
            var Q94;
            Q94=makeQuery(id+"F5.opPattern","COPY",BODY,{"derivedFrom":makeQuery(id+"F3.opExtrude","SWEPT_BODY",BODY,{"disambiguationData":[OSD([sQuery(id+"F2.wireOp",EDGE,"E2"),sQuery(id+"F2.wireOp",EDGE,"E3"),sQuery(id+"F2.wireOp",EDGE,"E4"),sQuery(id+"F2.wireOp",EDGE,"E5.filletArc"),sQuery(id+"F2.wireOp",EDGE,"E6.filletArc"),sQuery(id+"F2.wireOp",EDGE,"E7"),sQuery(id+"F2.wireOp",EDGE,"E8"),sQuery(id+"F2.wireOp",EDGE,"E10")])]}),"instanceName":"93"});
            var Q95;
            Q95=makeQuery(id+"F5.opPattern","COPY",BODY,{"derivedFrom":makeQuery(id+"F3.opExtrude","SWEPT_BODY",BODY,{"disambiguationData":[OSD([sQuery(id+"F2.wireOp",EDGE,"E2"),sQuery(id+"F2.wireOp",EDGE,"E3"),sQuery(id+"F2.wireOp",EDGE,"E4"),sQuery(id+"F2.wireOp",EDGE,"E5.filletArc"),sQuery(id+"F2.wireOp",EDGE,"E6.filletArc"),sQuery(id+"F2.wireOp",EDGE,"E7"),sQuery(id+"F2.wireOp",EDGE,"E8"),sQuery(id+"F2.wireOp",EDGE,"E10")])]}),"instanceName":"94"});
            var Q96;
            Q96=makeQuery(id+"F5.opPattern","COPY",BODY,{"derivedFrom":makeQuery(id+"F3.opExtrude","SWEPT_BODY",BODY,{"disambiguationData":[OSD([sQuery(id+"F2.wireOp",EDGE,"E2"),sQuery(id+"F2.wireOp",EDGE,"E3"),sQuery(id+"F2.wireOp",EDGE,"E4"),sQuery(id+"F2.wireOp",EDGE,"E5.filletArc"),sQuery(id+"F2.wireOp",EDGE,"E6.filletArc"),sQuery(id+"F2.wireOp",EDGE,"E7"),sQuery(id+"F2.wireOp",EDGE,"E8"),sQuery(id+"F2.wireOp",EDGE,"E10")])]}),"instanceName":"95"});
            var Q97;
            Q97=makeQuery(id+"F5.opPattern","COPY",BODY,{"derivedFrom":makeQuery(id+"F3.opExtrude","SWEPT_BODY",BODY,{"disambiguationData":[OSD([sQuery(id+"F2.wireOp",EDGE,"E2"),sQuery(id+"F2.wireOp",EDGE,"E3"),sQuery(id+"F2.wireOp",EDGE,"E4"),sQuery(id+"F2.wireOp",EDGE,"E5.filletArc"),sQuery(id+"F2.wireOp",EDGE,"E6.filletArc"),sQuery(id+"F2.wireOp",EDGE,"E7"),sQuery(id+"F2.wireOp",EDGE,"E8"),sQuery(id+"F2.wireOp",EDGE,"E10")])]}),"instanceName":"96"});
            var Q98;
            Q98=makeQuery(id+"F5.opPattern","COPY",BODY,{"derivedFrom":makeQuery(id+"F3.opExtrude","SWEPT_BODY",BODY,{"disambiguationData":[OSD([sQuery(id+"F2.wireOp",EDGE,"E2"),sQuery(id+"F2.wireOp",EDGE,"E3"),sQuery(id+"F2.wireOp",EDGE,"E4"),sQuery(id+"F2.wireOp",EDGE,"E5.filletArc"),sQuery(id+"F2.wireOp",EDGE,"E6.filletArc"),sQuery(id+"F2.wireOp",EDGE,"E7"),sQuery(id+"F2.wireOp",EDGE,"E8"),sQuery(id+"F2.wireOp",EDGE,"E10")])]}),"instanceName":"97"});
            var Q99;
            Q99=makeQuery(id+"F5.opPattern","COPY",BODY,{"derivedFrom":makeQuery(id+"F3.opExtrude","SWEPT_BODY",BODY,{"disambiguationData":[OSD([sQuery(id+"F2.wireOp",EDGE,"E2"),sQuery(id+"F2.wireOp",EDGE,"E3"),sQuery(id+"F2.wireOp",EDGE,"E4"),sQuery(id+"F2.wireOp",EDGE,"E5.filletArc"),sQuery(id+"F2.wireOp",EDGE,"E6.filletArc"),sQuery(id+"F2.wireOp",EDGE,"E7"),sQuery(id+"F2.wireOp",EDGE,"E8"),sQuery(id+"F2.wireOp",EDGE,"E10")])]}),"instanceName":"98"});
            var Q100;
            Q100=makeQuery(id+"F5.opPattern","COPY",BODY,{"derivedFrom":makeQuery(id+"F3.opExtrude","SWEPT_BODY",BODY,{"disambiguationData":[OSD([sQuery(id+"F2.wireOp",EDGE,"E2"),sQuery(id+"F2.wireOp",EDGE,"E3"),sQuery(id+"F2.wireOp",EDGE,"E4"),sQuery(id+"F2.wireOp",EDGE,"E5.filletArc"),sQuery(id+"F2.wireOp",EDGE,"E6.filletArc"),sQuery(id+"F2.wireOp",EDGE,"E7"),sQuery(id+"F2.wireOp",EDGE,"E8"),sQuery(id+"F2.wireOp",EDGE,"E10")])]}),"instanceName":"99"});
            var Q101;
            Q101=makeQuery(id+"F5.opPattern","COPY",BODY,{"derivedFrom":makeQuery(id+"F3.opExtrude","SWEPT_BODY",BODY,{"disambiguationData":[OSD([sQuery(id+"F2.wireOp",EDGE,"E2"),sQuery(id+"F2.wireOp",EDGE,"E3"),sQuery(id+"F2.wireOp",EDGE,"E4"),sQuery(id+"F2.wireOp",EDGE,"E5.filletArc"),sQuery(id+"F2.wireOp",EDGE,"E6.filletArc"),sQuery(id+"F2.wireOp",EDGE,"E7"),sQuery(id+"F2.wireOp",EDGE,"E8"),sQuery(id+"F2.wireOp",EDGE,"E10")])]}),"instanceName":"100"});
            var Q102;
            Q102=makeQuery(id+"F5.opPattern","COPY",BODY,{"derivedFrom":makeQuery(id+"F3.opExtrude","SWEPT_BODY",BODY,{"disambiguationData":[OSD([sQuery(id+"F2.wireOp",EDGE,"E2"),sQuery(id+"F2.wireOp",EDGE,"E3"),sQuery(id+"F2.wireOp",EDGE,"E4"),sQuery(id+"F2.wireOp",EDGE,"E5.filletArc"),sQuery(id+"F2.wireOp",EDGE,"E6.filletArc"),sQuery(id+"F2.wireOp",EDGE,"E7"),sQuery(id+"F2.wireOp",EDGE,"E8"),sQuery(id+"F2.wireOp",EDGE,"E10")])]}),"instanceName":"101"});
            var Q103;
            Q103=makeQuery(id+"F5.opPattern","COPY",BODY,{"derivedFrom":makeQuery(id+"F3.opExtrude","SWEPT_BODY",BODY,{"disambiguationData":[OSD([sQuery(id+"F2.wireOp",EDGE,"E2"),sQuery(id+"F2.wireOp",EDGE,"E3"),sQuery(id+"F2.wireOp",EDGE,"E4"),sQuery(id+"F2.wireOp",EDGE,"E5.filletArc"),sQuery(id+"F2.wireOp",EDGE,"E6.filletArc"),sQuery(id+"F2.wireOp",EDGE,"E7"),sQuery(id+"F2.wireOp",EDGE,"E8"),sQuery(id+"F2.wireOp",EDGE,"E10")])]}),"instanceName":"102"});
            var Q104;
            Q104=makeQuery(id+"F5.opPattern","COPY",BODY,{"derivedFrom":makeQuery(id+"F3.opExtrude","SWEPT_BODY",BODY,{"disambiguationData":[OSD([sQuery(id+"F2.wireOp",EDGE,"E2"),sQuery(id+"F2.wireOp",EDGE,"E3"),sQuery(id+"F2.wireOp",EDGE,"E4"),sQuery(id+"F2.wireOp",EDGE,"E5.filletArc"),sQuery(id+"F2.wireOp",EDGE,"E6.filletArc"),sQuery(id+"F2.wireOp",EDGE,"E7"),sQuery(id+"F2.wireOp",EDGE,"E8"),sQuery(id+"F2.wireOp",EDGE,"E10")])]}),"instanceName":"103"});
            var Q105;
            Q105=makeQuery(id+"F5.opPattern","COPY",BODY,{"derivedFrom":makeQuery(id+"F3.opExtrude","SWEPT_BODY",BODY,{"disambiguationData":[OSD([sQuery(id+"F2.wireOp",EDGE,"E2"),sQuery(id+"F2.wireOp",EDGE,"E3"),sQuery(id+"F2.wireOp",EDGE,"E4"),sQuery(id+"F2.wireOp",EDGE,"E5.filletArc"),sQuery(id+"F2.wireOp",EDGE,"E6.filletArc"),sQuery(id+"F2.wireOp",EDGE,"E7"),sQuery(id+"F2.wireOp",EDGE,"E8"),sQuery(id+"F2.wireOp",EDGE,"E10")])]}),"instanceName":"104"});
            var Q106;
            Q106=makeQuery(id+"F5.opPattern","COPY",BODY,{"derivedFrom":makeQuery(id+"F3.opExtrude","SWEPT_BODY",BODY,{"disambiguationData":[OSD([sQuery(id+"F2.wireOp",EDGE,"E2"),sQuery(id+"F2.wireOp",EDGE,"E3"),sQuery(id+"F2.wireOp",EDGE,"E4"),sQuery(id+"F2.wireOp",EDGE,"E5.filletArc"),sQuery(id+"F2.wireOp",EDGE,"E6.filletArc"),sQuery(id+"F2.wireOp",EDGE,"E7"),sQuery(id+"F2.wireOp",EDGE,"E8"),sQuery(id+"F2.wireOp",EDGE,"E10")])]}),"instanceName":"105"});
            var Q107;
            Q107=makeQuery(id+"F5.opPattern","COPY",BODY,{"derivedFrom":makeQuery(id+"F3.opExtrude","SWEPT_BODY",BODY,{"disambiguationData":[OSD([sQuery(id+"F2.wireOp",EDGE,"E2"),sQuery(id+"F2.wireOp",EDGE,"E3"),sQuery(id+"F2.wireOp",EDGE,"E4"),sQuery(id+"F2.wireOp",EDGE,"E5.filletArc"),sQuery(id+"F2.wireOp",EDGE,"E6.filletArc"),sQuery(id+"F2.wireOp",EDGE,"E7"),sQuery(id+"F2.wireOp",EDGE,"E8"),sQuery(id+"F2.wireOp",EDGE,"E10")])]}),"instanceName":"106"});
            var Q108;
            Q108=makeQuery(id+"F5.opPattern","COPY",BODY,{"derivedFrom":makeQuery(id+"F3.opExtrude","SWEPT_BODY",BODY,{"disambiguationData":[OSD([sQuery(id+"F2.wireOp",EDGE,"E2"),sQuery(id+"F2.wireOp",EDGE,"E3"),sQuery(id+"F2.wireOp",EDGE,"E4"),sQuery(id+"F2.wireOp",EDGE,"E5.filletArc"),sQuery(id+"F2.wireOp",EDGE,"E6.filletArc"),sQuery(id+"F2.wireOp",EDGE,"E7"),sQuery(id+"F2.wireOp",EDGE,"E8"),sQuery(id+"F2.wireOp",EDGE,"E10")])]}),"instanceName":"107"});
            var Q109;
            Q109=makeQuery(id+"F5.opPattern","COPY",BODY,{"derivedFrom":makeQuery(id+"F3.opExtrude","SWEPT_BODY",BODY,{"disambiguationData":[OSD([sQuery(id+"F2.wireOp",EDGE,"E2"),sQuery(id+"F2.wireOp",EDGE,"E3"),sQuery(id+"F2.wireOp",EDGE,"E4"),sQuery(id+"F2.wireOp",EDGE,"E5.filletArc"),sQuery(id+"F2.wireOp",EDGE,"E6.filletArc"),sQuery(id+"F2.wireOp",EDGE,"E7"),sQuery(id+"F2.wireOp",EDGE,"E8"),sQuery(id+"F2.wireOp",EDGE,"E10")])]}),"instanceName":"108"});
            var Q110;
            Q110=makeQuery(id+"F5.opPattern","COPY",BODY,{"derivedFrom":makeQuery(id+"F3.opExtrude","SWEPT_BODY",BODY,{"disambiguationData":[OSD([sQuery(id+"F2.wireOp",EDGE,"E2"),sQuery(id+"F2.wireOp",EDGE,"E3"),sQuery(id+"F2.wireOp",EDGE,"E4"),sQuery(id+"F2.wireOp",EDGE,"E5.filletArc"),sQuery(id+"F2.wireOp",EDGE,"E6.filletArc"),sQuery(id+"F2.wireOp",EDGE,"E7"),sQuery(id+"F2.wireOp",EDGE,"E8"),sQuery(id+"F2.wireOp",EDGE,"E10")])]}),"instanceName":"109"});
            var Q111;
            Q111=makeQuery(id+"F5.opPattern","COPY",BODY,{"derivedFrom":makeQuery(id+"F3.opExtrude","SWEPT_BODY",BODY,{"disambiguationData":[OSD([sQuery(id+"F2.wireOp",EDGE,"E2"),sQuery(id+"F2.wireOp",EDGE,"E3"),sQuery(id+"F2.wireOp",EDGE,"E4"),sQuery(id+"F2.wireOp",EDGE,"E5.filletArc"),sQuery(id+"F2.wireOp",EDGE,"E6.filletArc"),sQuery(id+"F2.wireOp",EDGE,"E7"),sQuery(id+"F2.wireOp",EDGE,"E8"),sQuery(id+"F2.wireOp",EDGE,"E10")])]}),"instanceName":"110"});
            var Q112;
            Q112=makeQuery(id+"F5.opPattern","COPY",BODY,{"derivedFrom":makeQuery(id+"F3.opExtrude","SWEPT_BODY",BODY,{"disambiguationData":[OSD([sQuery(id+"F2.wireOp",EDGE,"E2"),sQuery(id+"F2.wireOp",EDGE,"E3"),sQuery(id+"F2.wireOp",EDGE,"E4"),sQuery(id+"F2.wireOp",EDGE,"E5.filletArc"),sQuery(id+"F2.wireOp",EDGE,"E6.filletArc"),sQuery(id+"F2.wireOp",EDGE,"E7"),sQuery(id+"F2.wireOp",EDGE,"E8"),sQuery(id+"F2.wireOp",EDGE,"E10")])]}),"instanceName":"111"});
            var Q113;
            Q113=makeQuery(id+"F5.opPattern","COPY",BODY,{"derivedFrom":makeQuery(id+"F3.opExtrude","SWEPT_BODY",BODY,{"disambiguationData":[OSD([sQuery(id+"F2.wireOp",EDGE,"E2"),sQuery(id+"F2.wireOp",EDGE,"E3"),sQuery(id+"F2.wireOp",EDGE,"E4"),sQuery(id+"F2.wireOp",EDGE,"E5.filletArc"),sQuery(id+"F2.wireOp",EDGE,"E6.filletArc"),sQuery(id+"F2.wireOp",EDGE,"E7"),sQuery(id+"F2.wireOp",EDGE,"E8"),sQuery(id+"F2.wireOp",EDGE,"E10")])]}),"instanceName":"112"});
            var Q114;
            Q114=makeQuery(id+"F5.opPattern","COPY",BODY,{"derivedFrom":makeQuery(id+"F3.opExtrude","SWEPT_BODY",BODY,{"disambiguationData":[OSD([sQuery(id+"F2.wireOp",EDGE,"E2"),sQuery(id+"F2.wireOp",EDGE,"E3"),sQuery(id+"F2.wireOp",EDGE,"E4"),sQuery(id+"F2.wireOp",EDGE,"E5.filletArc"),sQuery(id+"F2.wireOp",EDGE,"E6.filletArc"),sQuery(id+"F2.wireOp",EDGE,"E7"),sQuery(id+"F2.wireOp",EDGE,"E8"),sQuery(id+"F2.wireOp",EDGE,"E10")])]}),"instanceName":"113"});
            var Q115;
            Q115=makeQuery(id+"F5.opPattern","COPY",BODY,{"derivedFrom":makeQuery(id+"F3.opExtrude","SWEPT_BODY",BODY,{"disambiguationData":[OSD([sQuery(id+"F2.wireOp",EDGE,"E2"),sQuery(id+"F2.wireOp",EDGE,"E3"),sQuery(id+"F2.wireOp",EDGE,"E4"),sQuery(id+"F2.wireOp",EDGE,"E5.filletArc"),sQuery(id+"F2.wireOp",EDGE,"E6.filletArc"),sQuery(id+"F2.wireOp",EDGE,"E7"),sQuery(id+"F2.wireOp",EDGE,"E8"),sQuery(id+"F2.wireOp",EDGE,"E10")])]}),"instanceName":"114"});
            var Q116;
            Q116=makeQuery(id+"F5.opPattern","COPY",BODY,{"derivedFrom":makeQuery(id+"F3.opExtrude","SWEPT_BODY",BODY,{"disambiguationData":[OSD([sQuery(id+"F2.wireOp",EDGE,"E2"),sQuery(id+"F2.wireOp",EDGE,"E3"),sQuery(id+"F2.wireOp",EDGE,"E4"),sQuery(id+"F2.wireOp",EDGE,"E5.filletArc"),sQuery(id+"F2.wireOp",EDGE,"E6.filletArc"),sQuery(id+"F2.wireOp",EDGE,"E7"),sQuery(id+"F2.wireOp",EDGE,"E8"),sQuery(id+"F2.wireOp",EDGE,"E10")])]}),"instanceName":"115"});
            var Q117;
            Q117=makeQuery(id+"F5.opPattern","COPY",BODY,{"derivedFrom":makeQuery(id+"F3.opExtrude","SWEPT_BODY",BODY,{"disambiguationData":[OSD([sQuery(id+"F2.wireOp",EDGE,"E2"),sQuery(id+"F2.wireOp",EDGE,"E3"),sQuery(id+"F2.wireOp",EDGE,"E4"),sQuery(id+"F2.wireOp",EDGE,"E5.filletArc"),sQuery(id+"F2.wireOp",EDGE,"E6.filletArc"),sQuery(id+"F2.wireOp",EDGE,"E7"),sQuery(id+"F2.wireOp",EDGE,"E8"),sQuery(id+"F2.wireOp",EDGE,"E10")])]}),"instanceName":"116"});
            var Q118;
            Q118=makeQuery(id+"F5.opPattern","COPY",BODY,{"derivedFrom":makeQuery(id+"F3.opExtrude","SWEPT_BODY",BODY,{"disambiguationData":[OSD([sQuery(id+"F2.wireOp",EDGE,"E2"),sQuery(id+"F2.wireOp",EDGE,"E3"),sQuery(id+"F2.wireOp",EDGE,"E4"),sQuery(id+"F2.wireOp",EDGE,"E5.filletArc"),sQuery(id+"F2.wireOp",EDGE,"E6.filletArc"),sQuery(id+"F2.wireOp",EDGE,"E7"),sQuery(id+"F2.wireOp",EDGE,"E8"),sQuery(id+"F2.wireOp",EDGE,"E10")])]}),"instanceName":"117"});
            var Q119;
            Q119=makeQuery(id+"F5.opPattern","COPY",BODY,{"derivedFrom":makeQuery(id+"F3.opExtrude","SWEPT_BODY",BODY,{"disambiguationData":[OSD([sQuery(id+"F2.wireOp",EDGE,"E2"),sQuery(id+"F2.wireOp",EDGE,"E3"),sQuery(id+"F2.wireOp",EDGE,"E4"),sQuery(id+"F2.wireOp",EDGE,"E5.filletArc"),sQuery(id+"F2.wireOp",EDGE,"E6.filletArc"),sQuery(id+"F2.wireOp",EDGE,"E7"),sQuery(id+"F2.wireOp",EDGE,"E8"),sQuery(id+"F2.wireOp",EDGE,"E10")])]}),"instanceName":"118"});
            var Q120;
            Q120=makeQuery(id+"F5.opPattern","COPY",BODY,{"derivedFrom":makeQuery(id+"F3.opExtrude","SWEPT_BODY",BODY,{"disambiguationData":[OSD([sQuery(id+"F2.wireOp",EDGE,"E2"),sQuery(id+"F2.wireOp",EDGE,"E3"),sQuery(id+"F2.wireOp",EDGE,"E4"),sQuery(id+"F2.wireOp",EDGE,"E5.filletArc"),sQuery(id+"F2.wireOp",EDGE,"E6.filletArc"),sQuery(id+"F2.wireOp",EDGE,"E7"),sQuery(id+"F2.wireOp",EDGE,"E8"),sQuery(id+"F2.wireOp",EDGE,"E10")])]}),"instanceName":"119"});
            var Q121;
            Q121=makeQuery(id+"F5.opPattern","COPY",BODY,{"derivedFrom":makeQuery(id+"F3.opExtrude","SWEPT_BODY",BODY,{"disambiguationData":[OSD([sQuery(id+"F2.wireOp",EDGE,"E2"),sQuery(id+"F2.wireOp",EDGE,"E3"),sQuery(id+"F2.wireOp",EDGE,"E4"),sQuery(id+"F2.wireOp",EDGE,"E5.filletArc"),sQuery(id+"F2.wireOp",EDGE,"E6.filletArc"),sQuery(id+"F2.wireOp",EDGE,"E7"),sQuery(id+"F2.wireOp",EDGE,"E8"),sQuery(id+"F2.wireOp",EDGE,"E10")])]}),"instanceName":"120"});
            var Q122;
            Q122=makeQuery(id+"F5.opPattern","COPY",BODY,{"derivedFrom":makeQuery(id+"F3.opExtrude","SWEPT_BODY",BODY,{"disambiguationData":[OSD([sQuery(id+"F2.wireOp",EDGE,"E2"),sQuery(id+"F2.wireOp",EDGE,"E3"),sQuery(id+"F2.wireOp",EDGE,"E4"),sQuery(id+"F2.wireOp",EDGE,"E5.filletArc"),sQuery(id+"F2.wireOp",EDGE,"E6.filletArc"),sQuery(id+"F2.wireOp",EDGE,"E7"),sQuery(id+"F2.wireOp",EDGE,"E8"),sQuery(id+"F2.wireOp",EDGE,"E10")])]}),"instanceName":"121"});
            var Q123;
            Q123=makeQuery(id+"F5.opPattern","COPY",BODY,{"derivedFrom":makeQuery(id+"F3.opExtrude","SWEPT_BODY",BODY,{"disambiguationData":[OSD([sQuery(id+"F2.wireOp",EDGE,"E2"),sQuery(id+"F2.wireOp",EDGE,"E3"),sQuery(id+"F2.wireOp",EDGE,"E4"),sQuery(id+"F2.wireOp",EDGE,"E5.filletArc"),sQuery(id+"F2.wireOp",EDGE,"E6.filletArc"),sQuery(id+"F2.wireOp",EDGE,"E7"),sQuery(id+"F2.wireOp",EDGE,"E8"),sQuery(id+"F2.wireOp",EDGE,"E10")])]}),"instanceName":"122"});
            var Q124;
            Q124=makeQuery(id+"F5.opPattern","COPY",BODY,{"derivedFrom":makeQuery(id+"F3.opExtrude","SWEPT_BODY",BODY,{"disambiguationData":[OSD([sQuery(id+"F2.wireOp",EDGE,"E2"),sQuery(id+"F2.wireOp",EDGE,"E3"),sQuery(id+"F2.wireOp",EDGE,"E4"),sQuery(id+"F2.wireOp",EDGE,"E5.filletArc"),sQuery(id+"F2.wireOp",EDGE,"E6.filletArc"),sQuery(id+"F2.wireOp",EDGE,"E7"),sQuery(id+"F2.wireOp",EDGE,"E8"),sQuery(id+"F2.wireOp",EDGE,"E10")])]}),"instanceName":"123"});
            var Q125;
            Q125=makeQuery(id+"F5.opPattern","COPY",BODY,{"derivedFrom":makeQuery(id+"F3.opExtrude","SWEPT_BODY",BODY,{"disambiguationData":[OSD([sQuery(id+"F2.wireOp",EDGE,"E2"),sQuery(id+"F2.wireOp",EDGE,"E3"),sQuery(id+"F2.wireOp",EDGE,"E4"),sQuery(id+"F2.wireOp",EDGE,"E5.filletArc"),sQuery(id+"F2.wireOp",EDGE,"E6.filletArc"),sQuery(id+"F2.wireOp",EDGE,"E7"),sQuery(id+"F2.wireOp",EDGE,"E8"),sQuery(id+"F2.wireOp",EDGE,"E10")])]}),"instanceName":"124"});
            var Q126;
            Q126=makeQuery(id+"F5.opPattern","COPY",BODY,{"derivedFrom":makeQuery(id+"F3.opExtrude","SWEPT_BODY",BODY,{"disambiguationData":[OSD([sQuery(id+"F2.wireOp",EDGE,"E2"),sQuery(id+"F2.wireOp",EDGE,"E3"),sQuery(id+"F2.wireOp",EDGE,"E4"),sQuery(id+"F2.wireOp",EDGE,"E5.filletArc"),sQuery(id+"F2.wireOp",EDGE,"E6.filletArc"),sQuery(id+"F2.wireOp",EDGE,"E7"),sQuery(id+"F2.wireOp",EDGE,"E8"),sQuery(id+"F2.wireOp",EDGE,"E10")])]}),"instanceName":"125"});
            var Q127;
            Q127=makeQuery(id+"F5.opPattern","COPY",BODY,{"derivedFrom":makeQuery(id+"F3.opExtrude","SWEPT_BODY",BODY,{"disambiguationData":[OSD([sQuery(id+"F2.wireOp",EDGE,"E2"),sQuery(id+"F2.wireOp",EDGE,"E3"),sQuery(id+"F2.wireOp",EDGE,"E4"),sQuery(id+"F2.wireOp",EDGE,"E5.filletArc"),sQuery(id+"F2.wireOp",EDGE,"E6.filletArc"),sQuery(id+"F2.wireOp",EDGE,"E7"),sQuery(id+"F2.wireOp",EDGE,"E8"),sQuery(id+"F2.wireOp",EDGE,"E10")])]}),"instanceName":"126"});
            var Q128;
            Q128=makeQuery(id+"F5.opPattern","COPY",BODY,{"derivedFrom":makeQuery(id+"F3.opExtrude","SWEPT_BODY",BODY,{"disambiguationData":[OSD([sQuery(id+"F2.wireOp",EDGE,"E2"),sQuery(id+"F2.wireOp",EDGE,"E3"),sQuery(id+"F2.wireOp",EDGE,"E4"),sQuery(id+"F2.wireOp",EDGE,"E5.filletArc"),sQuery(id+"F2.wireOp",EDGE,"E6.filletArc"),sQuery(id+"F2.wireOp",EDGE,"E7"),sQuery(id+"F2.wireOp",EDGE,"E8"),sQuery(id+"F2.wireOp",EDGE,"E10")])]}),"instanceName":"127"});
            booleanBodies(context, id + "F6", {"operationType" : BooleanOperationType.UNION, "tools" : qUnion([Q0, Q1, Q2, Q3, Q4, Q5, Q6, Q7, Q8, Q9, Q10, Q11, Q12, Q13, Q14, Q15, Q16, Q17, Q18, Q19, Q20, Q21, Q22, Q23, Q24, Q25, Q26, Q27, Q28, Q29, Q30, Q31, Q32, Q33, Q34, Q35, Q36, Q37, Q38, Q39, Q40, Q41, Q42, Q43, Q44, Q45, Q46, Q47, Q48, Q49, Q50, Q51, Q52, Q53, Q54, Q55, Q56, Q57, Q58, Q59, Q60, Q61, Q62, Q63, Q64, Q65, Q66, Q67, Q68, Q69, Q70, Q71, Q72, Q73, Q74, Q75, Q76, Q77, Q78, Q79, Q80, Q81, Q82, Q83, Q84, Q85, Q86, Q87, Q88, Q89, Q90, Q91, Q92, Q93, Q94, Q95, Q96, Q97, Q98, Q99, Q100, Q101, Q102, Q103, Q104, Q105, Q106, Q107, Q108, Q109, Q110, Q111, Q112, Q113, Q114, Q115, Q116, Q117, Q118, Q119, Q120, Q121, Q122, Q123, Q124, Q125, Q126, Q127, Q128])});
        }
        {
            var Q0;
            {var subQ0=sQuery(id+"F0.wireOp",EDGE,"E0");var subQ1=makeQuery(id+"F3.opExtrude","CAP_FACE",FACE,{"disambiguationData":[OSD([subQ0])],"isStart":false});Q0=makeQuery(id+"F6.opBoolean","MERGE",FACE,{"derivedFrom":[makeQuery(id+"F1.opExtrude","CAP_FACE",FACE,{"disambiguationData":[OSD([subQ0])],"isStart":false}),subQ1,makeQuery(id+"F5.opPattern","COPY",FACE,{"derivedFrom":subQ1,"instanceName":"1"}),makeQuery(id+"F5.opPattern","COPY",FACE,{"derivedFrom":subQ1,"instanceName":"2"}),makeQuery(id+"F5.opPattern","COPY",FACE,{"derivedFrom":subQ1,"instanceName":"3"}),makeQuery(id+"F5.opPattern","COPY",FACE,{"derivedFrom":subQ1,"instanceName":"4"}),makeQuery(id+"F5.opPattern","COPY",FACE,{"derivedFrom":subQ1,"instanceName":"5"}),makeQuery(id+"F5.opPattern","COPY",FACE,{"derivedFrom":subQ1,"instanceName":"6"}),makeQuery(id+"F5.opPattern","COPY",FACE,{"derivedFrom":subQ1,"instanceName":"7"}),makeQuery(id+"F5.opPattern","COPY",FACE,{"derivedFrom":subQ1,"instanceName":"8"}),makeQuery(id+"F5.opPattern","COPY",FACE,{"derivedFrom":subQ1,"instanceName":"9"}),makeQuery(id+"F5.opPattern","COPY",FACE,{"derivedFrom":subQ1,"instanceName":"10"}),makeQuery(id+"F5.opPattern","COPY",FACE,{"derivedFrom":subQ1,"instanceName":"11"}),makeQuery(id+"F5.opPattern","COPY",FACE,{"derivedFrom":subQ1,"instanceName":"12"}),makeQuery(id+"F5.opPattern","COPY",FACE,{"derivedFrom":subQ1,"instanceName":"13"}),makeQuery(id+"F5.opPattern","COPY",FACE,{"derivedFrom":subQ1,"instanceName":"14"}),makeQuery(id+"F5.opPattern","COPY",FACE,{"derivedFrom":subQ1,"instanceName":"15"}),makeQuery(id+"F5.opPattern","COPY",FACE,{"derivedFrom":subQ1,"instanceName":"16"}),makeQuery(id+"F5.opPattern","COPY",FACE,{"derivedFrom":subQ1,"instanceName":"17"}),makeQuery(id+"F5.opPattern","COPY",FACE,{"derivedFrom":subQ1,"instanceName":"18"}),makeQuery(id+"F5.opPattern","COPY",FACE,{"derivedFrom":subQ1,"instanceName":"19"}),makeQuery(id+"F5.opPattern","COPY",FACE,{"derivedFrom":subQ1,"instanceName":"20"}),makeQuery(id+"F5.opPattern","COPY",FACE,{"derivedFrom":subQ1,"instanceName":"21"}),makeQuery(id+"F5.opPattern","COPY",FACE,{"derivedFrom":subQ1,"instanceName":"22"}),makeQuery(id+"F5.opPattern","COPY",FACE,{"derivedFrom":subQ1,"instanceName":"23"}),makeQuery(id+"F5.opPattern","COPY",FACE,{"derivedFrom":subQ1,"instanceName":"24"}),makeQuery(id+"F5.opPattern","COPY",FACE,{"derivedFrom":subQ1,"instanceName":"25"}),makeQuery(id+"F5.opPattern","COPY",FACE,{"derivedFrom":subQ1,"instanceName":"26"}),makeQuery(id+"F5.opPattern","COPY",FACE,{"derivedFrom":subQ1,"instanceName":"27"}),makeQuery(id+"F5.opPattern","COPY",FACE,{"derivedFrom":subQ1,"instanceName":"28"}),makeQuery(id+"F5.opPattern","COPY",FACE,{"derivedFrom":subQ1,"instanceName":"29"}),makeQuery(id+"F5.opPattern","COPY",FACE,{"derivedFrom":subQ1,"instanceName":"30"}),makeQuery(id+"F5.opPattern","COPY",FACE,{"derivedFrom":subQ1,"instanceName":"31"}),makeQuery(id+"F5.opPattern","COPY",FACE,{"derivedFrom":subQ1,"instanceName":"32"}),makeQuery(id+"F5.opPattern","COPY",FACE,{"derivedFrom":subQ1,"instanceName":"33"}),makeQuery(id+"F5.opPattern","COPY",FACE,{"derivedFrom":subQ1,"instanceName":"34"}),makeQuery(id+"F5.opPattern","COPY",FACE,{"derivedFrom":subQ1,"instanceName":"35"}),makeQuery(id+"F5.opPattern","COPY",FACE,{"derivedFrom":subQ1,"instanceName":"36"}),makeQuery(id+"F5.opPattern","COPY",FACE,{"derivedFrom":subQ1,"instanceName":"37"}),makeQuery(id+"F5.opPattern","COPY",FACE,{"derivedFrom":subQ1,"instanceName":"38"}),makeQuery(id+"F5.opPattern","COPY",FACE,{"derivedFrom":subQ1,"instanceName":"39"}),makeQuery(id+"F5.opPattern","COPY",FACE,{"derivedFrom":subQ1,"instanceName":"40"}),makeQuery(id+"F5.opPattern","COPY",FACE,{"derivedFrom":subQ1,"instanceName":"41"}),makeQuery(id+"F5.opPattern","COPY",FACE,{"derivedFrom":subQ1,"instanceName":"42"}),makeQuery(id+"F5.opPattern","COPY",FACE,{"derivedFrom":subQ1,"instanceName":"43"}),makeQuery(id+"F5.opPattern","COPY",FACE,{"derivedFrom":subQ1,"instanceName":"44"}),makeQuery(id+"F5.opPattern","COPY",FACE,{"derivedFrom":subQ1,"instanceName":"45"}),makeQuery(id+"F5.opPattern","COPY",FACE,{"derivedFrom":subQ1,"instanceName":"46"}),makeQuery(id+"F5.opPattern","COPY",FACE,{"derivedFrom":subQ1,"instanceName":"47"}),makeQuery(id+"F5.opPattern","COPY",FACE,{"derivedFrom":subQ1,"instanceName":"48"}),makeQuery(id+"F5.opPattern","COPY",FACE,{"derivedFrom":subQ1,"instanceName":"49"}),makeQuery(id+"F5.opPattern","COPY",FACE,{"derivedFrom":subQ1,"instanceName":"50"}),makeQuery(id+"F5.opPattern","COPY",FACE,{"derivedFrom":subQ1,"instanceName":"51"}),makeQuery(id+"F5.opPattern","COPY",FACE,{"derivedFrom":subQ1,"instanceName":"52"}),makeQuery(id+"F5.opPattern","COPY",FACE,{"derivedFrom":subQ1,"instanceName":"53"}),makeQuery(id+"F5.opPattern","COPY",FACE,{"derivedFrom":subQ1,"instanceName":"54"}),makeQuery(id+"F5.opPattern","COPY",FACE,{"derivedFrom":subQ1,"instanceName":"55"}),makeQuery(id+"F5.opPattern","COPY",FACE,{"derivedFrom":subQ1,"instanceName":"56"}),makeQuery(id+"F5.opPattern","COPY",FACE,{"derivedFrom":subQ1,"instanceName":"57"}),makeQuery(id+"F5.opPattern","COPY",FACE,{"derivedFrom":subQ1,"instanceName":"58"}),makeQuery(id+"F5.opPattern","COPY",FACE,{"derivedFrom":subQ1,"instanceName":"59"}),makeQuery(id+"F5.opPattern","COPY",FACE,{"derivedFrom":subQ1,"instanceName":"60"}),makeQuery(id+"F5.opPattern","COPY",FACE,{"derivedFrom":subQ1,"instanceName":"61"}),makeQuery(id+"F5.opPattern","COPY",FACE,{"derivedFrom":subQ1,"instanceName":"62"}),makeQuery(id+"F5.opPattern","COPY",FACE,{"derivedFrom":subQ1,"instanceName":"63"}),makeQuery(id+"F5.opPattern","COPY",FACE,{"derivedFrom":subQ1,"instanceName":"64"}),makeQuery(id+"F5.opPattern","COPY",FACE,{"derivedFrom":subQ1,"instanceName":"65"}),makeQuery(id+"F5.opPattern","COPY",FACE,{"derivedFrom":subQ1,"instanceName":"66"}),makeQuery(id+"F5.opPattern","COPY",FACE,{"derivedFrom":subQ1,"instanceName":"67"}),makeQuery(id+"F5.opPattern","COPY",FACE,{"derivedFrom":subQ1,"instanceName":"68"}),makeQuery(id+"F5.opPattern","COPY",FACE,{"derivedFrom":subQ1,"instanceName":"69"}),makeQuery(id+"F5.opPattern","COPY",FACE,{"derivedFrom":subQ1,"instanceName":"70"}),makeQuery(id+"F5.opPattern","COPY",FACE,{"derivedFrom":subQ1,"instanceName":"71"}),makeQuery(id+"F5.opPattern","COPY",FACE,{"derivedFrom":subQ1,"instanceName":"72"}),makeQuery(id+"F5.opPattern","COPY",FACE,{"derivedFrom":subQ1,"instanceName":"73"}),makeQuery(id+"F5.opPattern","COPY",FACE,{"derivedFrom":subQ1,"instanceName":"74"}),makeQuery(id+"F5.opPattern","COPY",FACE,{"derivedFrom":subQ1,"instanceName":"75"}),makeQuery(id+"F5.opPattern","COPY",FACE,{"derivedFrom":subQ1,"instanceName":"76"}),makeQuery(id+"F5.opPattern","COPY",FACE,{"derivedFrom":subQ1,"instanceName":"77"}),makeQuery(id+"F5.opPattern","COPY",FACE,{"derivedFrom":subQ1,"instanceName":"78"}),makeQuery(id+"F5.opPattern","COPY",FACE,{"derivedFrom":subQ1,"instanceName":"79"}),makeQuery(id+"F5.opPattern","COPY",FACE,{"derivedFrom":subQ1,"instanceName":"80"}),makeQuery(id+"F5.opPattern","COPY",FACE,{"derivedFrom":subQ1,"instanceName":"81"}),makeQuery(id+"F5.opPattern","COPY",FACE,{"derivedFrom":subQ1,"instanceName":"82"}),makeQuery(id+"F5.opPattern","COPY",FACE,{"derivedFrom":subQ1,"instanceName":"83"}),makeQuery(id+"F5.opPattern","COPY",FACE,{"derivedFrom":subQ1,"instanceName":"84"}),makeQuery(id+"F5.opPattern","COPY",FACE,{"derivedFrom":subQ1,"instanceName":"85"}),makeQuery(id+"F5.opPattern","COPY",FACE,{"derivedFrom":subQ1,"instanceName":"86"}),makeQuery(id+"F5.opPattern","COPY",FACE,{"derivedFrom":subQ1,"instanceName":"87"}),makeQuery(id+"F5.opPattern","COPY",FACE,{"derivedFrom":subQ1,"instanceName":"88"}),makeQuery(id+"F5.opPattern","COPY",FACE,{"derivedFrom":subQ1,"instanceName":"89"}),makeQuery(id+"F5.opPattern","COPY",FACE,{"derivedFrom":subQ1,"instanceName":"90"}),makeQuery(id+"F5.opPattern","COPY",FACE,{"derivedFrom":subQ1,"instanceName":"91"}),makeQuery(id+"F5.opPattern","COPY",FACE,{"derivedFrom":subQ1,"instanceName":"92"}),makeQuery(id+"F5.opPattern","COPY",FACE,{"derivedFrom":subQ1,"instanceName":"93"}),makeQuery(id+"F5.opPattern","COPY",FACE,{"derivedFrom":subQ1,"instanceName":"94"}),makeQuery(id+"F5.opPattern","COPY",FACE,{"derivedFrom":subQ1,"instanceName":"95"}),makeQuery(id+"F5.opPattern","COPY",FACE,{"derivedFrom":subQ1,"instanceName":"96"}),makeQuery(id+"F5.opPattern","COPY",FACE,{"derivedFrom":subQ1,"instanceName":"97"}),makeQuery(id+"F5.opPattern","COPY",FACE,{"derivedFrom":subQ1,"instanceName":"98"}),makeQuery(id+"F5.opPattern","COPY",FACE,{"derivedFrom":subQ1,"instanceName":"99"}),makeQuery(id+"F5.opPattern","COPY",FACE,{"derivedFrom":subQ1,"instanceName":"100"}),makeQuery(id+"F5.opPattern","COPY",FACE,{"derivedFrom":subQ1,"instanceName":"101"}),makeQuery(id+"F5.opPattern","COPY",FACE,{"derivedFrom":subQ1,"instanceName":"102"}),makeQuery(id+"F5.opPattern","COPY",FACE,{"derivedFrom":subQ1,"instanceName":"103"}),makeQuery(id+"F5.opPattern","COPY",FACE,{"derivedFrom":subQ1,"instanceName":"104"}),makeQuery(id+"F5.opPattern","COPY",FACE,{"derivedFrom":subQ1,"instanceName":"105"}),makeQuery(id+"F5.opPattern","COPY",FACE,{"derivedFrom":subQ1,"instanceName":"106"}),makeQuery(id+"F5.opPattern","COPY",FACE,{"derivedFrom":subQ1,"instanceName":"107"}),makeQuery(id+"F5.opPattern","COPY",FACE,{"derivedFrom":subQ1,"instanceName":"108"}),makeQuery(id+"F5.opPattern","COPY",FACE,{"derivedFrom":subQ1,"instanceName":"109"}),makeQuery(id+"F5.opPattern","COPY",FACE,{"derivedFrom":subQ1,"instanceName":"110"}),makeQuery(id+"F5.opPattern","COPY",FACE,{"derivedFrom":subQ1,"instanceName":"111"}),makeQuery(id+"F5.opPattern","COPY",FACE,{"derivedFrom":subQ1,"instanceName":"112"}),makeQuery(id+"F5.opPattern","COPY",FACE,{"derivedFrom":subQ1,"instanceName":"113"}),makeQuery(id+"F5.opPattern","COPY",FACE,{"derivedFrom":subQ1,"instanceName":"114"}),makeQuery(id+"F5.opPattern","COPY",FACE,{"derivedFrom":subQ1,"instanceName":"115"}),makeQuery(id+"F5.opPattern","COPY",FACE,{"derivedFrom":subQ1,"instanceName":"116"}),makeQuery(id+"F5.opPattern","COPY",FACE,{"derivedFrom":subQ1,"instanceName":"117"}),makeQuery(id+"F5.opPattern","COPY",FACE,{"derivedFrom":subQ1,"instanceName":"118"}),makeQuery(id+"F5.opPattern","COPY",FACE,{"derivedFrom":subQ1,"instanceName":"119"}),makeQuery(id+"F5.opPattern","COPY",FACE,{"derivedFrom":subQ1,"instanceName":"120"}),makeQuery(id+"F5.opPattern","COPY",FACE,{"derivedFrom":subQ1,"instanceName":"121"}),makeQuery(id+"F5.opPattern","COPY",FACE,{"derivedFrom":subQ1,"instanceName":"122"}),makeQuery(id+"F5.opPattern","COPY",FACE,{"derivedFrom":subQ1,"instanceName":"123"}),makeQuery(id+"F5.opPattern","COPY",FACE,{"derivedFrom":subQ1,"instanceName":"124"}),makeQuery(id+"F5.opPattern","COPY",FACE,{"derivedFrom":subQ1,"instanceName":"125"}),makeQuery(id+"F5.opPattern","COPY",FACE,{"derivedFrom":subQ1,"instanceName":"126"}),makeQuery(id+"F5.opPattern","COPY",FACE,{"derivedFrom":subQ1,"instanceName":"127"})]});}
            var sketch = newSketch(context, id + "F7", { "sketchPlane" : qUnion([Q0])});
            skCircle(sketch, "E12", {"center": v(0, 0) * mm, "radius": 30.23 * mm});
            skSolve(sketch);
        }
        {
            var Q0;
            Q0 = qSketchRegion(id + "F7", true);
            extrude(context, id + "F8", {"entities" : qUnion([Q0]), "operationType" : NewBodyOperationType.REMOVE, "oppositeDirection" : true, "depth" : 25.4 * mm});
        }
    });
